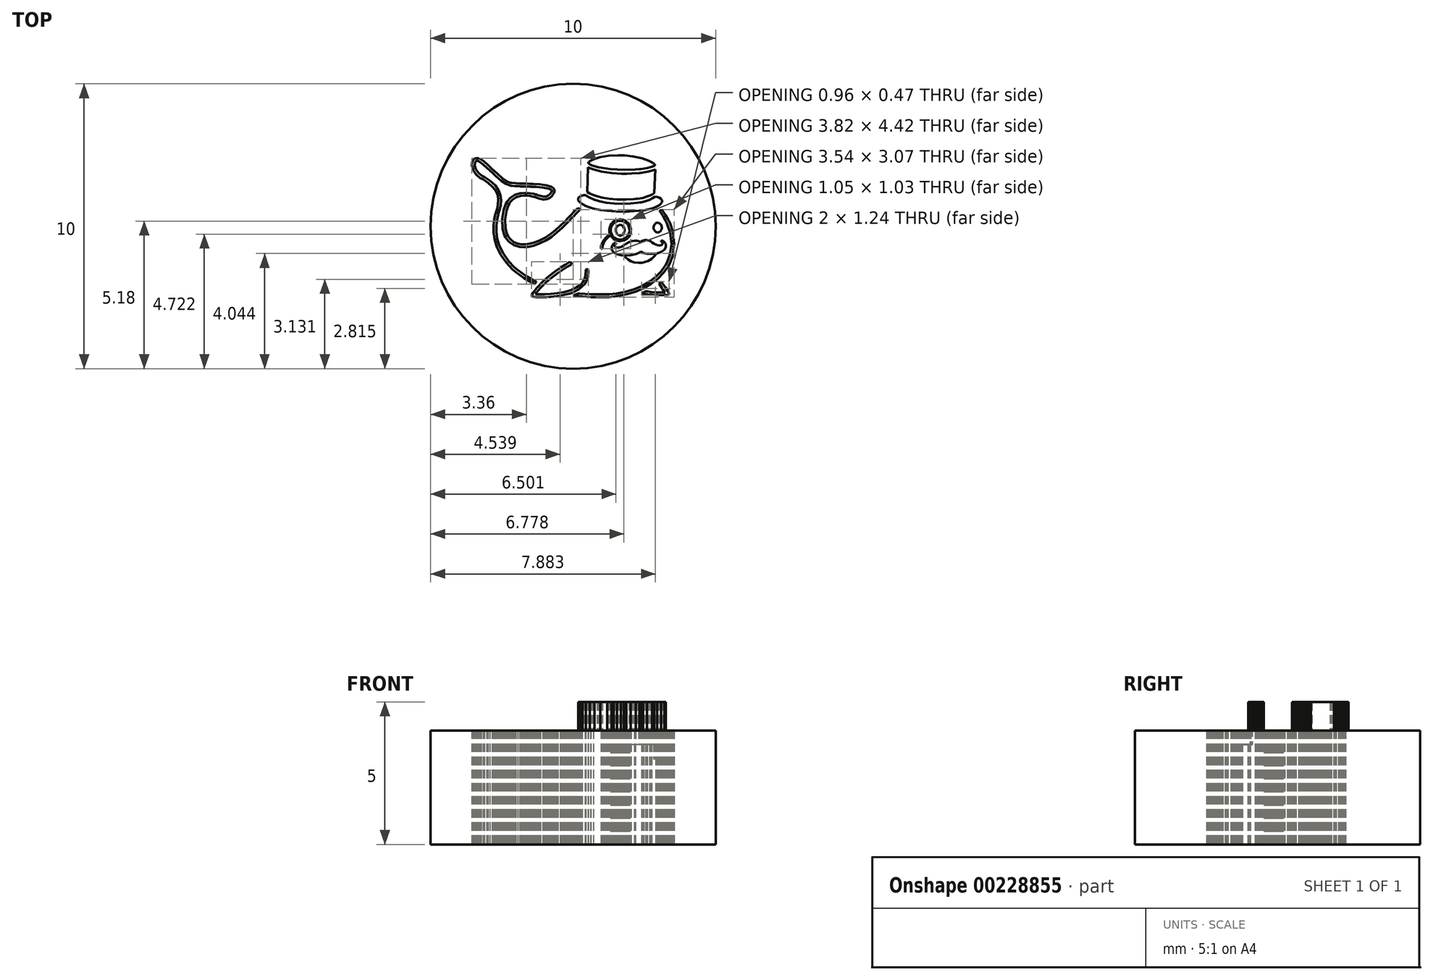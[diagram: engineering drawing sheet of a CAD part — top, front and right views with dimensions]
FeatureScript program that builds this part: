
annotation { "Feature Type Name" : "Feature", "Feature Type Description" : "" }
export const myFeature = defineFeature(function(context is Context, id is Id, definition is map)
    precondition{}
    {
        {
            var Q0;
            Q0=qCreatedBy(makeId("Top.planeOp"),FACE);
            var sketch = newSketch(context, id + "F0", { "sketchPlane" : qUnion([Q0])});
            skLineSegment(sketch, "E0", {"start": v(2.92, -0.96) * mm, "end": v(2.85, -1.06) * mm});
            skLineSegment(sketch, "E1", {"start": v(2.85, -1.06) * mm, "end": v(2.75, -1.15) * mm});
            skLineSegment(sketch, "E2", {"start": v(2.75, -1.15) * mm, "end": v(2.62, -1.22) * mm});
            skLineSegment(sketch, "E3", {"start": v(2.62, -1.22) * mm, "end": v(2.5, -1.26) * mm});
            skLineSegment(sketch, "E4", {"start": v(2.5, -1.26) * mm, "end": v(2.46, -1.27) * mm});
            skLineSegment(sketch, "E5", {"start": v(2.46, -1.27) * mm, "end": v(2.42, -1.28) * mm});
            skLineSegment(sketch, "E6", {"start": v(2.42, -1.28) * mm, "end": v(2.3, -1.29) * mm});
            skLineSegment(sketch, "E7", {"start": v(2.3, -1.29) * mm, "end": v(2.15, -1.27) * mm});
            skLineSegment(sketch, "E8", {"start": v(2.15, -1.27) * mm, "end": v(2.03, -1.23) * mm});
            skLineSegment(sketch, "E9", {"start": v(2.03, -1.23) * mm, "end": v(1.93, -1.17) * mm});
            skLineSegment(sketch, "E10", {"start": v(1.93, -1.17) * mm, "end": v(1.84, -1.1) * mm});
            skLineSegment(sketch, "E11", {"start": v(-1.26, -2.49) * mm, "end": v(-1.26, -2.49) * mm});
            skLineSegment(sketch, "E12", {"start": v(-1.26, -2.49) * mm, "end": v(-1.28, -2.48) * mm});
            skLineSegment(sketch, "E13", {"start": v(-1.28, -2.48) * mm, "end": v(-1.29, -2.48) * mm});
            skLineSegment(sketch, "E14", {"start": v(-1.29, -2.48) * mm, "end": v(-1.3, -2.48) * mm});
            skLineSegment(sketch, "E15", {"start": v(-1.3, -2.48) * mm, "end": v(-1.37, -2.48) * mm});
            skLineSegment(sketch, "E16", {"start": v(-1.37, -2.48) * mm, "end": v(-1.42, -2.47) * mm});
            skLineSegment(sketch, "E17", {"start": v(-1.42, -2.47) * mm, "end": v(-1.44, -2.46) * mm});
            skLineSegment(sketch, "E18", {"start": v(-1.44, -2.46) * mm, "end": v(-1.45, -2.45) * mm});
            skLineSegment(sketch, "E19", {"start": v(-1.45, -2.45) * mm, "end": v(-1.45, -2.45) * mm});
            skLineSegment(sketch, "E20", {"start": v(-1.45, -2.45) * mm, "end": v(-1.46, -2.42) * mm});
            skLineSegment(sketch, "E21", {"start": v(-1.46, -2.42) * mm, "end": v(-1.45, -2.4) * mm});
            skLineSegment(sketch, "E22", {"start": v(-1.45, -2.4) * mm, "end": v(-1.4, -2.34) * mm});
            skLineSegment(sketch, "E23", {"start": v(-1.4, -2.34) * mm, "end": v(-1.27, -2.16) * mm});
            skLineSegment(sketch, "E24", {"start": v(-1.27, -2.16) * mm, "end": v(-1.07, -1.94) * mm});
            skLineSegment(sketch, "E25", {"start": v(-1.07, -1.94) * mm, "end": v(-0.85, -1.75) * mm});
            skLineSegment(sketch, "E26", {"start": v(-0.85, -1.75) * mm, "end": v(-0.63, -1.58) * mm});
            skLineSegment(sketch, "E27", {"start": v(-0.63, -1.58) * mm, "end": v(-0.43, -1.45) * mm});
            skLineSegment(sketch, "E28", {"start": v(-0.43, -1.45) * mm, "end": v(-0.26, -1.34) * mm});
            skLineSegment(sketch, "E29", {"start": v(-0.26, -1.34) * mm, "end": v(-0.15, -1.28) * mm});
            skLineSegment(sketch, "E30", {"start": v(-0.15, -1.28) * mm, "end": v(-0.1, -1.25) * mm});
            skLineSegment(sketch, "E31", {"start": v(-0.1, -1.25) * mm, "end": v(-0.1, -1.25) * mm});
            skLineSegment(sketch, "E32", {"start": v(-0.1, -1.25) * mm, "end": v(-0.05, -1.33) * mm});
            skLineSegment(sketch, "E33", {"start": v(-0.05, -1.33) * mm, "end": v(-0.05, -1.34) * mm});
            skLineSegment(sketch, "E34", {"start": v(-0.05, -1.34) * mm, "end": v(-0.1, -1.36) * mm});
            skLineSegment(sketch, "E35", {"start": v(-0.1, -1.36) * mm, "end": v(-0.2, -1.42) * mm});
            skLineSegment(sketch, "E36", {"start": v(-0.2, -1.42) * mm, "end": v(-0.35, -1.5) * mm});
            skLineSegment(sketch, "E37", {"start": v(-0.35, -1.5) * mm, "end": v(-0.53, -1.63) * mm});
            skLineSegment(sketch, "E38", {"start": v(-0.53, -1.63) * mm, "end": v(-0.74, -1.79) * mm});
            skLineSegment(sketch, "E39", {"start": v(-0.74, -1.79) * mm, "end": v(-0.95, -1.97) * mm});
            skLineSegment(sketch, "E40", {"start": v(-0.95, -1.97) * mm, "end": v(-1.15, -2.17) * mm});
            skLineSegment(sketch, "E41", {"start": v(-1.15, -2.17) * mm, "end": v(-1.28, -2.33) * mm});
            skLineSegment(sketch, "E42", {"start": v(-1.28, -2.33) * mm, "end": v(-1.32, -2.39) * mm});
            skLineSegment(sketch, "E43", {"start": v(-1.32, -2.39) * mm, "end": v(-1.29, -2.39) * mm});
            skLineSegment(sketch, "E44", {"start": v(-1.29, -2.39) * mm, "end": v(-1.19, -2.4) * mm});
            skLineSegment(sketch, "E45", {"start": v(-1.19, -2.4) * mm, "end": v(-1, -2.4) * mm});
            skLineSegment(sketch, "E46", {"start": v(-1, -2.4) * mm, "end": v(-0.8, -2.38) * mm});
            skLineSegment(sketch, "E47", {"start": v(-0.8, -2.38) * mm, "end": v(-0.56, -2.36) * mm});
            skLineSegment(sketch, "E48", {"start": v(-0.56, -2.36) * mm, "end": v(-0.32, -2.31) * mm});
            skLineSegment(sketch, "E49", {"start": v(-0.32, -2.31) * mm, "end": v(-0.09, -2.25) * mm});
            skLineSegment(sketch, "E50", {"start": v(-0.09, -2.25) * mm, "end": v(0.12, -2.15) * mm});
            skLineSegment(sketch, "E51", {"start": v(0.12, -2.15) * mm, "end": v(0.25, -2.07) * mm});
            skLineSegment(sketch, "E52", {"start": v(0.25, -2.07) * mm, "end": v(0.29, -2.03) * mm});
            skLineSegment(sketch, "E53", {"start": v(0.29, -2.03) * mm, "end": v(0.32, -2) * mm});
            skLineSegment(sketch, "E54", {"start": v(0.32, -2) * mm, "end": v(0.42, -1.8) * mm});
            skLineSegment(sketch, "E55", {"start": v(0.42, -1.8) * mm, "end": v(0.44, -1.57) * mm});
            skLineSegment(sketch, "E56", {"start": v(0.44, -1.57) * mm, "end": v(0.43, -1.52) * mm});
            skLineSegment(sketch, "E57", {"start": v(0.43, -1.52) * mm, "end": v(0.53, -1.5) * mm});
            skLineSegment(sketch, "E58", {"start": v(0.53, -1.5) * mm, "end": v(0.54, -1.57) * mm});
            skLineSegment(sketch, "E59", {"start": v(0.54, -1.57) * mm, "end": v(0.53, -1.78) * mm});
            skLineSegment(sketch, "E60", {"start": v(0.53, -1.78) * mm, "end": v(0.42, -2.02) * mm});
            skLineSegment(sketch, "E61", {"start": v(0.42, -2.02) * mm, "end": v(0.2, -2.21) * mm});
            skLineSegment(sketch, "E62", {"start": v(0.2, -2.21) * mm, "end": v(-0.03, -2.33) * mm});
            skLineSegment(sketch, "E63", {"start": v(-0.03, -2.33) * mm, "end": v(-0.12, -2.36) * mm});
            skLineSegment(sketch, "E64", {"start": v(-0.12, -2.36) * mm, "end": v(-0.17, -2.38) * mm});
            skLineSegment(sketch, "E65", {"start": v(-0.17, -2.38) * mm, "end": v(-0.34, -2.42) * mm});
            skLineSegment(sketch, "E66", {"start": v(-0.34, -2.42) * mm, "end": v(-0.57, -2.45) * mm});
            skLineSegment(sketch, "E67", {"start": v(-0.57, -2.45) * mm, "end": v(-0.78, -2.48) * mm});
            skLineSegment(sketch, "E68", {"start": v(-0.78, -2.48) * mm, "end": v(-0.92, -2.48) * mm});
            skLineSegment(sketch, "E69", {"start": v(-0.92, -2.48) * mm, "end": v(-0.97, -2.49) * mm});
            skLineSegment(sketch, "E70", {"start": v(-0.97, -2.49) * mm, "end": v(-1, -2.49) * mm});
            skLineSegment(sketch, "E71", {"start": v(-1, -2.49) * mm, "end": v(-1.14, -2.49) * mm});
            skLineSegment(sketch, "E72", {"start": v(-1.14, -2.49) * mm, "end": v(-1.24, -2.49) * mm});
            skLineSegment(sketch, "E73", {"start": v(-1.24, -2.49) * mm, "end": v(-1.26, -2.49) * mm});
            skLineSegment(sketch, "E74", {"start": v(3.36, -2.34) * mm, "end": v(3.34, -2.3) * mm});
            skLineSegment(sketch, "E75", {"start": v(3.34, -2.3) * mm, "end": v(3.23, -2.14) * mm});
            skLineSegment(sketch, "E76", {"start": v(3.23, -2.14) * mm, "end": v(3.12, -1.98) * mm});
            skLineSegment(sketch, "E77", {"start": v(3.12, -1.98) * mm, "end": v(3.1, -1.95) * mm});
            skLineSegment(sketch, "E78", {"start": v(3.1, -1.95) * mm, "end": v(3.09, -1.96) * mm});
            skLineSegment(sketch, "E79", {"start": v(3.09, -1.96) * mm, "end": v(3.02, -2.01) * mm});
            skLineSegment(sketch, "E80", {"start": v(3.02, -2.01) * mm, "end": v(3.01, -2.02) * mm});
            skLineSegment(sketch, "E81", {"start": v(3.01, -2.02) * mm, "end": v(3.03, -2.04) * mm});
            skLineSegment(sketch, "E82", {"start": v(3.03, -2.04) * mm, "end": v(3.2, -2.3) * mm});
            skLineSegment(sketch, "E83", {"start": v(3.2, -2.3) * mm, "end": v(3.22, -2.32) * mm});
            skLineSegment(sketch, "E84", {"start": v(3.22, -2.32) * mm, "end": v(3.2, -2.32) * mm});
            skLineSegment(sketch, "E85", {"start": v(3.2, -2.32) * mm, "end": v(3.1, -2.32) * mm});
            skLineSegment(sketch, "E86", {"start": v(3.1, -2.32) * mm, "end": v(2.94, -2.32) * mm});
            skLineSegment(sketch, "E87", {"start": v(2.94, -2.32) * mm, "end": v(2.75, -2.3) * mm});
            skLineSegment(sketch, "E88", {"start": v(2.75, -2.3) * mm, "end": v(2.6, -2.3) * mm});
            skLineSegment(sketch, "E89", {"start": v(2.6, -2.3) * mm, "end": v(2.55, -2.28) * mm});
            skLineSegment(sketch, "E90", {"start": v(2.55, -2.28) * mm, "end": v(2.54, -2.3) * mm});
            skLineSegment(sketch, "E91", {"start": v(2.54, -2.3) * mm, "end": v(2.41, -2.35) * mm});
            skLineSegment(sketch, "E92", {"start": v(2.41, -2.35) * mm, "end": v(2.4, -2.35) * mm});
            skLineSegment(sketch, "E93", {"start": v(2.4, -2.35) * mm, "end": v(2.43, -2.36) * mm});
            skLineSegment(sketch, "E94", {"start": v(2.43, -2.36) * mm, "end": v(2.7, -2.4) * mm});
            skLineSegment(sketch, "E95", {"start": v(2.7, -2.4) * mm, "end": v(2.73, -2.4) * mm});
            skLineSegment(sketch, "E96", {"start": v(2.73, -2.4) * mm, "end": v(2.75, -2.4) * mm});
            skLineSegment(sketch, "E97", {"start": v(2.75, -2.4) * mm, "end": v(2.91, -2.42) * mm});
            skLineSegment(sketch, "E98", {"start": v(2.91, -2.42) * mm, "end": v(2.93, -2.42) * mm});
            skLineSegment(sketch, "E99", {"start": v(2.93, -2.42) * mm, "end": v(2.96, -2.42) * mm});
            skLineSegment(sketch, "E100", {"start": v(2.96, -2.42) * mm, "end": v(3.09, -2.42) * mm});
            skLineSegment(sketch, "E101", {"start": v(3.09, -2.42) * mm, "end": v(3.19, -2.42) * mm});
            skLineSegment(sketch, "E102", {"start": v(3.19, -2.42) * mm, "end": v(3.2, -2.42) * mm});
            skLineSegment(sketch, "E103", {"start": v(3.2, -2.42) * mm, "end": v(3.22, -2.42) * mm});
            skLineSegment(sketch, "E104", {"start": v(3.22, -2.42) * mm, "end": v(3.28, -2.42) * mm});
            skLineSegment(sketch, "E105", {"start": v(3.28, -2.42) * mm, "end": v(3.32, -2.41) * mm});
            skLineSegment(sketch, "E106", {"start": v(3.32, -2.41) * mm, "end": v(3.35, -2.4) * mm});
            skLineSegment(sketch, "E107", {"start": v(3.35, -2.4) * mm, "end": v(3.36, -2.4) * mm});
            skLineSegment(sketch, "E108", {"start": v(3.36, -2.4) * mm, "end": v(3.36, -2.39) * mm});
            skLineSegment(sketch, "E109", {"start": v(3.36, -2.39) * mm, "end": v(3.36, -2.39) * mm});
            skLineSegment(sketch, "E110", {"start": v(3.36, -2.39) * mm, "end": v(3.36, -2.35) * mm});
            skLineSegment(sketch, "E111", {"start": v(3.36, -2.35) * mm, "end": v(3.36, -2.34) * mm});
            skLineSegment(sketch, "E112", {"start": v(0.27, 0.6) * mm, "end": v(0.26, 0.6) * mm});
            skLineSegment(sketch, "E113", {"start": v(0.26, 0.6) * mm, "end": v(0.18, 0.64) * mm});
            skLineSegment(sketch, "E114", {"start": v(0.18, 0.64) * mm, "end": v(0.17, 0.64) * mm});
            skLineSegment(sketch, "E115", {"start": v(0.17, 0.64) * mm, "end": v(0.15, 0.62) * mm});
            skLineSegment(sketch, "E116", {"start": v(0.15, 0.62) * mm, "end": v(0.09, 0.56) * mm});
            skLineSegment(sketch, "E117", {"start": v(0.09, 0.56) * mm, "end": v(0.02, 0.5) * mm});
            skLineSegment(sketch, "E118", {"start": v(0.02, 0.5) * mm, "end": v(-0.05, 0.42) * mm});
            skLineSegment(sketch, "E119", {"start": v(-0.05, 0.42) * mm, "end": v(-0.12, 0.35) * mm});
            skLineSegment(sketch, "E120", {"start": v(-0.12, 0.35) * mm, "end": v(-0.14, 0.33) * mm});
            skLineSegment(sketch, "E121", {"start": v(-0.14, 0.33) * mm, "end": v(-0.18, 0.29) * mm});
            skLineSegment(sketch, "E122", {"start": v(-0.18, 0.29) * mm, "end": v(-0.3, 0.17) * mm});
            skLineSegment(sketch, "E123", {"start": v(-0.3, 0.17) * mm, "end": v(-0.45, 0.01) * mm});
            skLineSegment(sketch, "E124", {"start": v(-0.45, 0.01) * mm, "end": v(-0.62, -0.14) * mm});
            skLineSegment(sketch, "E125", {"start": v(-0.62, -0.14) * mm, "end": v(-0.8, -0.28) * mm});
            skLineSegment(sketch, "E126", {"start": v(-0.8, -0.28) * mm, "end": v(-1, -0.4) * mm});
            skLineSegment(sketch, "E127", {"start": v(-1, -0.4) * mm, "end": v(-1.2, -0.51) * mm});
            skLineSegment(sketch, "E128", {"start": v(-1.2, -0.51) * mm, "end": v(-1.41, -0.59) * mm});
            skLineSegment(sketch, "E129", {"start": v(-1.41, -0.59) * mm, "end": v(-1.59, -0.62) * mm});
            skLineSegment(sketch, "E130", {"start": v(-1.59, -0.62) * mm, "end": v(-1.65, -0.63) * mm});
            skLineSegment(sketch, "E131", {"start": v(-1.65, -0.63) * mm, "end": v(-1.66, -0.63) * mm});
            skLineSegment(sketch, "E132", {"start": v(-1.66, -0.63) * mm, "end": v(-1.77, -0.64) * mm});
            skLineSegment(sketch, "E133", {"start": v(-1.77, -0.64) * mm, "end": v(-1.78, -0.63) * mm});
            skLineSegment(sketch, "E134", {"start": v(-1.78, -0.63) * mm, "end": v(-1.82, -0.63) * mm});
            skLineSegment(sketch, "E135", {"start": v(-1.82, -0.63) * mm, "end": v(-1.95, -0.61) * mm});
            skLineSegment(sketch, "E136", {"start": v(-1.95, -0.61) * mm, "end": v(-2.08, -0.55) * mm});
            skLineSegment(sketch, "E137", {"start": v(-2.08, -0.55) * mm, "end": v(-2.2, -0.46) * mm});
            skLineSegment(sketch, "E138", {"start": v(-2.2, -0.46) * mm, "end": v(-2.27, -0.37) * mm});
            skLineSegment(sketch, "E139", {"start": v(-2.27, -0.37) * mm, "end": v(-2.29, -0.34) * mm});
            skLineSegment(sketch, "E140", {"start": v(-2.29, -0.34) * mm, "end": v(-2.32, -0.28) * mm});
            skLineSegment(sketch, "E141", {"start": v(-2.32, -0.28) * mm, "end": v(-2.38, -0.07) * mm});
            skLineSegment(sketch, "E142", {"start": v(-2.38, -0.07) * mm, "end": v(-2.4, 0.24) * mm});
            skLineSegment(sketch, "E143", {"start": v(-2.4, 0.24) * mm, "end": v(-2.34, 0.54) * mm});
            skLineSegment(sketch, "E144", {"start": v(-2.34, 0.54) * mm, "end": v(-2.27, 0.74) * mm});
            skLineSegment(sketch, "E145", {"start": v(-2.27, 0.74) * mm, "end": v(-2.24, 0.8) * mm});
            skLineSegment(sketch, "E146", {"start": v(-2.24, 0.8) * mm, "end": v(-2.22, 0.83) * mm});
            skLineSegment(sketch, "E147", {"start": v(-2.22, 0.83) * mm, "end": v(-2.14, 0.93) * mm});
            skLineSegment(sketch, "E148", {"start": v(-2.14, 0.93) * mm, "end": v(-2, 1.01) * mm});
            skLineSegment(sketch, "E149", {"start": v(-2, 1.01) * mm, "end": v(-1.84, 1.06) * mm});
            skLineSegment(sketch, "E150", {"start": v(-1.84, 1.06) * mm, "end": v(-1.7, 1.08) * mm});
            skLineSegment(sketch, "E151", {"start": v(-1.7, 1.08) * mm, "end": v(-1.64, 1.08) * mm});
            skLineSegment(sketch, "E152", {"start": v(-1.64, 1.08) * mm, "end": v(-1.61, 1.07) * mm});
            skLineSegment(sketch, "E153", {"start": v(-1.61, 1.07) * mm, "end": v(-1.52, 1.06) * mm});
            skLineSegment(sketch, "E154", {"start": v(-1.52, 1.06) * mm, "end": v(-1.42, 1.05) * mm});
            skLineSegment(sketch, "E155", {"start": v(-1.42, 1.05) * mm, "end": v(-1.35, 1.03) * mm});
            skLineSegment(sketch, "E156", {"start": v(-1.35, 1.03) * mm, "end": v(-1.33, 1.02) * mm});
            skLineSegment(sketch, "E157", {"start": v(-1.33, 1.02) * mm, "end": v(-1.33, 1.02) * mm});
            skLineSegment(sketch, "E158", {"start": v(-1.33, 1.02) * mm, "end": v(-1.3, 1.01) * mm});
            skLineSegment(sketch, "E159", {"start": v(-1.3, 1.01) * mm, "end": v(-1.28, 1) * mm});
            skLineSegment(sketch, "E160", {"start": v(-1.28, 1) * mm, "end": v(-1.17, 0.97) * mm});
            skLineSegment(sketch, "E161", {"start": v(-1.17, 0.97) * mm, "end": v(-1.05, 0.94) * mm});
            skLineSegment(sketch, "E162", {"start": v(-1.05, 0.94) * mm, "end": v(-1.03, 0.94) * mm});
            skLineSegment(sketch, "E163", {"start": v(-1.03, 0.94) * mm, "end": v(-1, 0.94) * mm});
            skLineSegment(sketch, "E164", {"start": v(-1, 0.94) * mm, "end": v(-0.92, 0.95) * mm});
            skLineSegment(sketch, "E165", {"start": v(-0.92, 0.95) * mm, "end": v(-0.83, 0.99) * mm});
            skLineSegment(sketch, "E166", {"start": v(-0.83, 0.99) * mm, "end": v(-0.75, 1.06) * mm});
            skLineSegment(sketch, "E167", {"start": v(-0.75, 1.06) * mm, "end": v(-0.7, 1.13) * mm});
            skLineSegment(sketch, "E168", {"start": v(-0.7, 1.13) * mm, "end": v(-0.68, 1.15) * mm});
            skLineSegment(sketch, "E169", {"start": v(-0.68, 1.15) * mm, "end": v(-0.67, 1.16) * mm});
            skLineSegment(sketch, "E170", {"start": v(-0.67, 1.16) * mm, "end": v(-0.66, 1.2) * mm});
            skLineSegment(sketch, "E171", {"start": v(-0.66, 1.2) * mm, "end": v(-0.65, 1.24) * mm});
            skLineSegment(sketch, "E172", {"start": v(-0.65, 1.24) * mm, "end": v(-0.66, 1.28) * mm});
            skLineSegment(sketch, "E173", {"start": v(-0.66, 1.28) * mm, "end": v(-0.66, 1.3) * mm});
            skLineSegment(sketch, "E174", {"start": v(-0.66, 1.3) * mm, "end": v(-0.67, 1.3) * mm});
            skLineSegment(sketch, "E175", {"start": v(-0.67, 1.3) * mm, "end": v(-0.68, 1.33) * mm});
            skLineSegment(sketch, "E176", {"start": v(-0.68, 1.33) * mm, "end": v(-0.76, 1.39) * mm});
            skLineSegment(sketch, "E177", {"start": v(-0.76, 1.39) * mm, "end": v(-0.93, 1.44) * mm});
            skLineSegment(sketch, "E178", {"start": v(-0.93, 1.44) * mm, "end": v(-1.17, 1.47) * mm});
            skLineSegment(sketch, "E179", {"start": v(-1.17, 1.47) * mm, "end": v(-1.4, 1.48) * mm});
            skLineSegment(sketch, "E180", {"start": v(-1.4, 1.48) * mm, "end": v(-1.47, 1.49) * mm});
            skLineSegment(sketch, "E181", {"start": v(-1.47, 1.49) * mm, "end": v(-1.49, 1.49) * mm});
            skLineSegment(sketch, "E182", {"start": v(-1.49, 1.49) * mm, "end": v(-1.65, 1.5) * mm});
            skLineSegment(sketch, "E183", {"start": v(-1.65, 1.5) * mm, "end": v(-1.66, 1.5) * mm});
            skLineSegment(sketch, "E184", {"start": v(-1.66, 1.5) * mm, "end": v(-1.68, 1.5) * mm});
            skLineSegment(sketch, "E185", {"start": v(-1.68, 1.5) * mm, "end": v(-1.82, 1.5) * mm});
            skLineSegment(sketch, "E186", {"start": v(-1.82, 1.5) * mm, "end": v(-1.84, 1.5) * mm});
            skLineSegment(sketch, "E187", {"start": v(-1.84, 1.5) * mm, "end": v(-1.86, 1.5) * mm});
            skLineSegment(sketch, "E188", {"start": v(-1.86, 1.5) * mm, "end": v(-2, 1.5) * mm});
            skLineSegment(sketch, "E189", {"start": v(-2, 1.5) * mm, "end": v(-2.14, 1.52) * mm});
            skLineSegment(sketch, "E190", {"start": v(-2.14, 1.52) * mm, "end": v(-2.17, 1.52) * mm});
            skLineSegment(sketch, "E191", {"start": v(-2.17, 1.52) * mm, "end": v(-2.2, 1.53) * mm});
            skLineSegment(sketch, "E192", {"start": v(-2.2, 1.53) * mm, "end": v(-2.32, 1.58) * mm});
            skLineSegment(sketch, "E193", {"start": v(-2.32, 1.58) * mm, "end": v(-2.48, 1.7) * mm});
            skLineSegment(sketch, "E194", {"start": v(-2.48, 1.7) * mm, "end": v(-2.66, 1.84) * mm});
            skLineSegment(sketch, "E195", {"start": v(-2.66, 1.84) * mm, "end": v(-2.78, 1.96) * mm});
            skLineSegment(sketch, "E196", {"start": v(-2.78, 1.96) * mm, "end": v(-2.83, 2) * mm});
            skLineSegment(sketch, "E197", {"start": v(-2.83, 2) * mm, "end": v(-2.86, 2.04) * mm});
            skLineSegment(sketch, "E198", {"start": v(-2.86, 2.04) * mm, "end": v(-2.98, 2.15) * mm});
            skLineSegment(sketch, "E199", {"start": v(-2.98, 2.15) * mm, "end": v(-3.13, 2.27) * mm});
            skLineSegment(sketch, "E200", {"start": v(-3.13, 2.27) * mm, "end": v(-3.25, 2.36) * mm});
            skLineSegment(sketch, "E201", {"start": v(-3.25, 2.36) * mm, "end": v(-3.34, 2.39) * mm});
            skLineSegment(sketch, "E202", {"start": v(-3.34, 2.39) * mm, "end": v(-3.37, 2.39) * mm});
            skLineSegment(sketch, "E203", {"start": v(-3.37, 2.39) * mm, "end": v(-3.38, 2.4) * mm});
            skLineSegment(sketch, "E204", {"start": v(-3.38, 2.4) * mm, "end": v(-3.4, 2.39) * mm});
            skLineSegment(sketch, "E205", {"start": v(-3.4, 2.39) * mm, "end": v(-3.45, 2.37) * mm});
            skLineSegment(sketch, "E206", {"start": v(-3.45, 2.37) * mm, "end": v(-3.49, 2.34) * mm});
            skLineSegment(sketch, "E207", {"start": v(-3.49, 2.34) * mm, "end": v(-3.52, 2.3) * mm});
            skLineSegment(sketch, "E208", {"start": v(-3.52, 2.3) * mm, "end": v(-3.52, 2.28) * mm});
            skLineSegment(sketch, "E209", {"start": v(-3.52, 2.28) * mm, "end": v(-3.54, 2.25) * mm});
            skLineSegment(sketch, "E210", {"start": v(-3.54, 2.25) * mm, "end": v(-3.55, 2.14) * mm});
            skLineSegment(sketch, "E211", {"start": v(-3.55, 2.14) * mm, "end": v(-3.5, 1.97) * mm});
            skLineSegment(sketch, "E212", {"start": v(-3.5, 1.97) * mm, "end": v(-3.4, 1.81) * mm});
            skLineSegment(sketch, "E213", {"start": v(-3.4, 1.81) * mm, "end": v(-3.28, 1.7) * mm});
            skLineSegment(sketch, "E214", {"start": v(-3.28, 1.7) * mm, "end": v(-3.23, 1.68) * mm});
            skLineSegment(sketch, "E215", {"start": v(-3.23, 1.68) * mm, "end": v(-3.17, 1.65) * mm});
            skLineSegment(sketch, "E216", {"start": v(-3.17, 1.65) * mm, "end": v(-2.99, 1.53) * mm});
            skLineSegment(sketch, "E217", {"start": v(-2.99, 1.53) * mm, "end": v(-2.81, 1.38) * mm});
            skLineSegment(sketch, "E218", {"start": v(-2.81, 1.38) * mm, "end": v(-2.7, 1.23) * mm});
            skLineSegment(sketch, "E219", {"start": v(-2.7, 1.23) * mm, "end": v(-2.64, 1.07) * mm});
            skLineSegment(sketch, "E220", {"start": v(-2.64, 1.07) * mm, "end": v(-2.63, 0.92) * mm});
            skLineSegment(sketch, "E221", {"start": v(-2.63, 0.92) * mm, "end": v(-2.64, 0.77) * mm});
            skLineSegment(sketch, "E222", {"start": v(-2.64, 0.77) * mm, "end": v(-2.67, 0.61) * mm});
            skLineSegment(sketch, "E223", {"start": v(-2.67, 0.61) * mm, "end": v(-2.7, 0.5) * mm});
            skLineSegment(sketch, "E224", {"start": v(-2.7, 0.5) * mm, "end": v(-2.71, 0.46) * mm});
            skLineSegment(sketch, "E225", {"start": v(-2.71, 0.46) * mm, "end": v(-2.73, 0.42) * mm});
            skLineSegment(sketch, "E226", {"start": v(-2.73, 0.42) * mm, "end": v(-2.74, 0.37) * mm});
            skLineSegment(sketch, "E227", {"start": v(-2.74, 0.37) * mm, "end": v(-2.77, 0.24) * mm});
            skLineSegment(sketch, "E228", {"start": v(-2.77, 0.24) * mm, "end": v(-2.8, 0.03) * mm});
            skLineSegment(sketch, "E229", {"start": v(-2.8, 0.03) * mm, "end": v(-2.8, -0.2) * mm});
            skLineSegment(sketch, "E230", {"start": v(-2.8, -0.2) * mm, "end": v(-2.76, -0.45) * mm});
            skLineSegment(sketch, "E231", {"start": v(-2.76, -0.45) * mm, "end": v(-2.68, -0.72) * mm});
            skLineSegment(sketch, "E232", {"start": v(-2.68, -0.72) * mm, "end": v(-2.54, -1) * mm});
            skLineSegment(sketch, "E233", {"start": v(-2.54, -1) * mm, "end": v(-2.34, -1.29) * mm});
            skLineSegment(sketch, "E234", {"start": v(-2.34, -1.29) * mm, "end": v(-2.13, -1.5) * mm});
            skLineSegment(sketch, "E235", {"start": v(-2.13, -1.5) * mm, "end": v(-2.06, -1.57) * mm});
            skLineSegment(sketch, "E236", {"start": v(-2.06, -1.57) * mm, "end": v(-2, -1.62) * mm});
            skLineSegment(sketch, "E237", {"start": v(-2, -1.62) * mm, "end": v(-1.73, -1.82) * mm});
            skLineSegment(sketch, "E238", {"start": v(-1.73, -1.82) * mm, "end": v(-1.42, -2) * mm});
            skLineSegment(sketch, "E239", {"start": v(-1.42, -2) * mm, "end": v(-1.35, -2.03) * mm});
            skLineSegment(sketch, "E240", {"start": v(-1.35, -2.03) * mm, "end": v(-1.35, -2.02) * mm});
            skLineSegment(sketch, "E241", {"start": v(-1.35, -2.02) * mm, "end": v(-1.3, -1.96) * mm});
            skLineSegment(sketch, "E242", {"start": v(-1.3, -1.96) * mm, "end": v(-1.3, -1.95) * mm});
            skLineSegment(sketch, "E243", {"start": v(-1.3, -1.95) * mm, "end": v(-1.36, -1.92) * mm});
            skLineSegment(sketch, "E244", {"start": v(-1.36, -1.92) * mm, "end": v(-1.67, -1.74) * mm});
            skLineSegment(sketch, "E245", {"start": v(-1.67, -1.74) * mm, "end": v(-1.94, -1.54) * mm});
            skLineSegment(sketch, "E246", {"start": v(-1.94, -1.54) * mm, "end": v(-2, -1.5) * mm});
            skLineSegment(sketch, "E247", {"start": v(-2, -1.5) * mm, "end": v(-2.06, -1.44) * mm});
            skLineSegment(sketch, "E248", {"start": v(-2.06, -1.44) * mm, "end": v(-2.26, -1.23) * mm});
            skLineSegment(sketch, "E249", {"start": v(-2.26, -1.23) * mm, "end": v(-2.45, -0.96) * mm});
            skLineSegment(sketch, "E250", {"start": v(-2.45, -0.96) * mm, "end": v(-2.59, -0.7) * mm});
            skLineSegment(sketch, "E251", {"start": v(-2.59, -0.7) * mm, "end": v(-2.66, -0.44) * mm});
            skLineSegment(sketch, "E252", {"start": v(-2.66, -0.44) * mm, "end": v(-2.7, -0.2) * mm});
            skLineSegment(sketch, "E253", {"start": v(-2.7, -0.2) * mm, "end": v(-2.7, 0.03) * mm});
            skLineSegment(sketch, "E254", {"start": v(-2.7, 0.03) * mm, "end": v(-2.67, 0.22) * mm});
            skLineSegment(sketch, "E255", {"start": v(-2.67, 0.22) * mm, "end": v(-2.64, 0.35) * mm});
            skLineSegment(sketch, "E256", {"start": v(-2.64, 0.35) * mm, "end": v(-2.63, 0.39) * mm});
            skLineSegment(sketch, "E257", {"start": v(-2.63, 0.39) * mm, "end": v(-2.62, 0.43) * mm});
            skLineSegment(sketch, "E258", {"start": v(-2.62, 0.43) * mm, "end": v(-2.6, 0.47) * mm});
            skLineSegment(sketch, "E259", {"start": v(-2.6, 0.47) * mm, "end": v(-2.58, 0.59) * mm});
            skLineSegment(sketch, "E260", {"start": v(-2.58, 0.59) * mm, "end": v(-2.54, 0.75) * mm});
            skLineSegment(sketch, "E261", {"start": v(-2.54, 0.75) * mm, "end": v(-2.53, 0.92) * mm});
            skLineSegment(sketch, "E262", {"start": v(-2.53, 0.92) * mm, "end": v(-2.55, 1.09) * mm});
            skLineSegment(sketch, "E263", {"start": v(-2.55, 1.09) * mm, "end": v(-2.61, 1.26) * mm});
            skLineSegment(sketch, "E264", {"start": v(-2.61, 1.26) * mm, "end": v(-2.73, 1.43) * mm});
            skLineSegment(sketch, "E265", {"start": v(-2.73, 1.43) * mm, "end": v(-2.92, 1.6) * mm});
            skLineSegment(sketch, "E266", {"start": v(-2.92, 1.6) * mm, "end": v(-3.11, 1.73) * mm});
            skLineSegment(sketch, "E267", {"start": v(-3.11, 1.73) * mm, "end": v(-3.18, 1.76) * mm});
            skLineSegment(sketch, "E268", {"start": v(-3.18, 1.76) * mm, "end": v(-3.22, 1.79) * mm});
            skLineSegment(sketch, "E269", {"start": v(-3.22, 1.79) * mm, "end": v(-3.33, 1.88) * mm});
            skLineSegment(sketch, "E270", {"start": v(-3.33, 1.88) * mm, "end": v(-3.42, 2) * mm});
            skLineSegment(sketch, "E271", {"start": v(-3.42, 2) * mm, "end": v(-3.45, 2.14) * mm});
            skLineSegment(sketch, "E272", {"start": v(-3.45, 2.14) * mm, "end": v(-3.45, 2.22) * mm});
            skLineSegment(sketch, "E273", {"start": v(-3.45, 2.22) * mm, "end": v(-3.44, 2.24) * mm});
            skLineSegment(sketch, "E274", {"start": v(-3.44, 2.24) * mm, "end": v(-3.43, 2.25) * mm});
            skLineSegment(sketch, "E275", {"start": v(-3.43, 2.25) * mm, "end": v(-3.4, 2.29) * mm});
            skLineSegment(sketch, "E276", {"start": v(-3.4, 2.29) * mm, "end": v(-3.38, 2.3) * mm});
            skLineSegment(sketch, "E277", {"start": v(-3.38, 2.3) * mm, "end": v(-3.37, 2.3) * mm});
            skLineSegment(sketch, "E278", {"start": v(-3.37, 2.3) * mm, "end": v(-3.35, 2.3) * mm});
            skLineSegment(sketch, "E279", {"start": v(-3.35, 2.3) * mm, "end": v(-3.28, 2.26) * mm});
            skLineSegment(sketch, "E280", {"start": v(-3.28, 2.26) * mm, "end": v(-3.16, 2.18) * mm});
            skLineSegment(sketch, "E281", {"start": v(-3.16, 2.18) * mm, "end": v(-3.03, 2.06) * mm});
            skLineSegment(sketch, "E282", {"start": v(-3.03, 2.06) * mm, "end": v(-2.93, 1.96) * mm});
            skLineSegment(sketch, "E283", {"start": v(-2.93, 1.96) * mm, "end": v(-2.9, 1.93) * mm});
            skLineSegment(sketch, "E284", {"start": v(-2.9, 1.93) * mm, "end": v(-2.85, 1.89) * mm});
            skLineSegment(sketch, "E285", {"start": v(-2.85, 1.89) * mm, "end": v(-2.7, 1.76) * mm});
            skLineSegment(sketch, "E286", {"start": v(-2.7, 1.76) * mm, "end": v(-2.53, 1.6) * mm});
            skLineSegment(sketch, "E287", {"start": v(-2.53, 1.6) * mm, "end": v(-2.35, 1.48) * mm});
            skLineSegment(sketch, "E288", {"start": v(-2.35, 1.48) * mm, "end": v(-2.22, 1.43) * mm});
            skLineSegment(sketch, "E289", {"start": v(-2.22, 1.43) * mm, "end": v(-2.18, 1.43) * mm});
            skLineSegment(sketch, "E290", {"start": v(-2.18, 1.43) * mm, "end": v(-2.16, 1.42) * mm});
            skLineSegment(sketch, "E291", {"start": v(-2.16, 1.42) * mm, "end": v(-2.04, 1.41) * mm});
            skLineSegment(sketch, "E292", {"start": v(-2.04, 1.41) * mm, "end": v(-1.88, 1.4) * mm});
            skLineSegment(sketch, "E293", {"start": v(-1.88, 1.4) * mm, "end": v(-1.84, 1.4) * mm});
            skLineSegment(sketch, "E294", {"start": v(-1.84, 1.4) * mm, "end": v(-1.83, 1.4) * mm});
            skLineSegment(sketch, "E295", {"start": v(-1.83, 1.4) * mm, "end": v(-1.68, 1.4) * mm});
            skLineSegment(sketch, "E296", {"start": v(-1.68, 1.4) * mm, "end": v(-1.67, 1.4) * mm});
            skLineSegment(sketch, "E297", {"start": v(-1.67, 1.4) * mm, "end": v(-1.65, 1.4) * mm});
            skLineSegment(sketch, "E298", {"start": v(-1.65, 1.4) * mm, "end": v(-1.5, 1.4) * mm});
            skLineSegment(sketch, "E299", {"start": v(-1.5, 1.4) * mm, "end": v(-1.48, 1.39) * mm});
            skLineSegment(sketch, "E300", {"start": v(-1.48, 1.39) * mm, "end": v(-1.43, 1.39) * mm});
            skLineSegment(sketch, "E301", {"start": v(-1.43, 1.39) * mm, "end": v(-1.3, 1.38) * mm});
            skLineSegment(sketch, "E302", {"start": v(-1.3, 1.38) * mm, "end": v(-1.07, 1.36) * mm});
            skLineSegment(sketch, "E303", {"start": v(-1.07, 1.36) * mm, "end": v(-0.86, 1.32) * mm});
            skLineSegment(sketch, "E304", {"start": v(-0.86, 1.32) * mm, "end": v(-0.77, 1.28) * mm});
            skLineSegment(sketch, "E305", {"start": v(-0.77, 1.28) * mm, "end": v(-0.75, 1.26) * mm});
            skLineSegment(sketch, "E306", {"start": v(-0.75, 1.26) * mm, "end": v(-0.75, 1.26) * mm});
            skLineSegment(sketch, "E307", {"start": v(-0.75, 1.26) * mm, "end": v(-0.75, 1.24) * mm});
            skLineSegment(sketch, "E308", {"start": v(-0.75, 1.24) * mm, "end": v(-0.76, 1.2) * mm});
            skLineSegment(sketch, "E309", {"start": v(-0.76, 1.2) * mm, "end": v(-0.76, 1.2) * mm});
            skLineSegment(sketch, "E310", {"start": v(-0.76, 1.2) * mm, "end": v(-0.77, 1.18) * mm});
            skLineSegment(sketch, "E311", {"start": v(-0.77, 1.18) * mm, "end": v(-0.82, 1.13) * mm});
            skLineSegment(sketch, "E312", {"start": v(-0.82, 1.13) * mm, "end": v(-0.88, 1.07) * mm});
            skLineSegment(sketch, "E313", {"start": v(-0.88, 1.07) * mm, "end": v(-0.95, 1.05) * mm});
            skLineSegment(sketch, "E314", {"start": v(-0.95, 1.05) * mm, "end": v(-1, 1.04) * mm});
            skLineSegment(sketch, "E315", {"start": v(-1, 1.04) * mm, "end": v(-1.02, 1.04) * mm});
            skLineSegment(sketch, "E316", {"start": v(-1.02, 1.04) * mm, "end": v(-1.04, 1.04) * mm});
            skLineSegment(sketch, "E317", {"start": v(-1.04, 1.04) * mm, "end": v(-1.15, 1.06) * mm});
            skLineSegment(sketch, "E318", {"start": v(-1.15, 1.06) * mm, "end": v(-1.25, 1.1) * mm});
            skLineSegment(sketch, "E319", {"start": v(-1.25, 1.1) * mm, "end": v(-1.27, 1.1) * mm});
            skLineSegment(sketch, "E320", {"start": v(-1.27, 1.1) * mm, "end": v(-1.3, 1.11) * mm});
            skLineSegment(sketch, "E321", {"start": v(-1.3, 1.11) * mm, "end": v(-1.3, 1.11) * mm});
            skLineSegment(sketch, "E322", {"start": v(-1.3, 1.11) * mm, "end": v(-1.32, 1.12) * mm});
            skLineSegment(sketch, "E323", {"start": v(-1.32, 1.12) * mm, "end": v(-1.4, 1.14) * mm});
            skLineSegment(sketch, "E324", {"start": v(-1.4, 1.14) * mm, "end": v(-1.5, 1.16) * mm});
            skLineSegment(sketch, "E325", {"start": v(-1.5, 1.16) * mm, "end": v(-1.6, 1.17) * mm});
            skLineSegment(sketch, "E326", {"start": v(-1.6, 1.17) * mm, "end": v(-1.64, 1.17) * mm});
            skLineSegment(sketch, "E327", {"start": v(-1.64, 1.17) * mm, "end": v(-1.7, 1.17) * mm});
            skLineSegment(sketch, "E328", {"start": v(-1.7, 1.17) * mm, "end": v(-1.86, 1.16) * mm});
            skLineSegment(sketch, "E329", {"start": v(-1.86, 1.16) * mm, "end": v(-2.05, 1.1) * mm});
            skLineSegment(sketch, "E330", {"start": v(-2.05, 1.1) * mm, "end": v(-2.2, 1) * mm});
            skLineSegment(sketch, "E331", {"start": v(-2.2, 1) * mm, "end": v(-2.3, 0.89) * mm});
            skLineSegment(sketch, "E332", {"start": v(-2.3, 0.89) * mm, "end": v(-2.32, 0.85) * mm});
            skLineSegment(sketch, "E333", {"start": v(-2.32, 0.85) * mm, "end": v(-2.36, 0.78) * mm});
            skLineSegment(sketch, "E334", {"start": v(-2.36, 0.78) * mm, "end": v(-2.43, 0.57) * mm});
            skLineSegment(sketch, "E335", {"start": v(-2.43, 0.57) * mm, "end": v(-2.49, 0.25) * mm});
            skLineSegment(sketch, "E336", {"start": v(-2.49, 0.25) * mm, "end": v(-2.47, -0.08) * mm});
            skLineSegment(sketch, "E337", {"start": v(-2.47, -0.08) * mm, "end": v(-2.41, -0.32) * mm});
            skLineSegment(sketch, "E338", {"start": v(-2.41, -0.32) * mm, "end": v(-2.37, -0.39) * mm});
            skLineSegment(sketch, "E339", {"start": v(-2.37, -0.39) * mm, "end": v(-2.35, -0.43) * mm});
            skLineSegment(sketch, "E340", {"start": v(-2.35, -0.43) * mm, "end": v(-2.25, -0.55) * mm});
            skLineSegment(sketch, "E341", {"start": v(-2.25, -0.55) * mm, "end": v(-2.08, -0.66) * mm});
            skLineSegment(sketch, "E342", {"start": v(-2.08, -0.66) * mm, "end": v(-1.87, -0.72) * mm});
            skLineSegment(sketch, "E343", {"start": v(-1.87, -0.72) * mm, "end": v(-1.7, -0.73) * mm});
            skLineSegment(sketch, "E344", {"start": v(-1.7, -0.73) * mm, "end": v(-1.64, -0.73) * mm});
            skLineSegment(sketch, "E345", {"start": v(-1.64, -0.73) * mm, "end": v(-1.57, -0.72) * mm});
            skLineSegment(sketch, "E346", {"start": v(-1.57, -0.72) * mm, "end": v(-1.4, -0.68) * mm});
            skLineSegment(sketch, "E347", {"start": v(-1.4, -0.68) * mm, "end": v(-1.16, -0.6) * mm});
            skLineSegment(sketch, "E348", {"start": v(-1.16, -0.6) * mm, "end": v(-0.95, -0.5) * mm});
            skLineSegment(sketch, "E349", {"start": v(-0.95, -0.5) * mm, "end": v(-0.75, -0.37) * mm});
            skLineSegment(sketch, "E350", {"start": v(-0.75, -0.37) * mm, "end": v(-0.57, -0.22) * mm});
            skLineSegment(sketch, "E351", {"start": v(-0.57, -0.22) * mm, "end": v(-0.4, -0.06) * mm});
            skLineSegment(sketch, "E352", {"start": v(-0.4, -0.06) * mm, "end": v(-0.23, 0.1) * mm});
            skLineSegment(sketch, "E353", {"start": v(-0.23, 0.1) * mm, "end": v(-0.1, 0.22) * mm});
            skLineSegment(sketch, "E354", {"start": v(-0.1, 0.22) * mm, "end": v(-0.07, 0.26) * mm});
            skLineSegment(sketch, "E355", {"start": v(-0.07, 0.26) * mm, "end": v(-0.05, 0.29) * mm});
            skLineSegment(sketch, "E356", {"start": v(-0.05, 0.29) * mm, "end": v(0.02, 0.36) * mm});
            skLineSegment(sketch, "E357", {"start": v(0.02, 0.36) * mm, "end": v(0.1, 0.44) * mm});
            skLineSegment(sketch, "E358", {"start": v(0.1, 0.44) * mm, "end": v(0.18, 0.52) * mm});
            skLineSegment(sketch, "E359", {"start": v(0.18, 0.52) * mm, "end": v(0.25, 0.58) * mm});
            skLineSegment(sketch, "E360", {"start": v(0.25, 0.58) * mm, "end": v(0.27, 0.6) * mm});
            skLineSegment(sketch, "E361", {"start": v(3.12, 0.58) * mm, "end": v(3.1, 0.58) * mm});
            skLineSegment(sketch, "E362", {"start": v(3.1, 0.58) * mm, "end": v(3.03, 0.55) * mm});
            skLineSegment(sketch, "E363", {"start": v(3.03, 0.55) * mm, "end": v(3.02, 0.54) * mm});
            skLineSegment(sketch, "E364", {"start": v(3.02, 0.54) * mm, "end": v(3.04, 0.52) * mm});
            skLineSegment(sketch, "E365", {"start": v(3.04, 0.52) * mm, "end": v(3.15, 0.36) * mm});
            skLineSegment(sketch, "E366", {"start": v(3.15, 0.36) * mm, "end": v(3.25, 0.2) * mm});
            skLineSegment(sketch, "E367", {"start": v(3.25, 0.2) * mm, "end": v(3.26, 0.16) * mm});
            skLineSegment(sketch, "E368", {"start": v(3.26, 0.16) * mm, "end": v(3.3, 0.07) * mm});
            skLineSegment(sketch, "E369", {"start": v(3.3, 0.07) * mm, "end": v(3.4, -0.24) * mm});
            skLineSegment(sketch, "E370", {"start": v(3.4, -0.24) * mm, "end": v(3.45, -0.63) * mm});
            skLineSegment(sketch, "E371", {"start": v(3.45, -0.63) * mm, "end": v(3.4, -1) * mm});
            skLineSegment(sketch, "E372", {"start": v(3.4, -1) * mm, "end": v(3.3, -1.29) * mm});
            skLineSegment(sketch, "E373", {"start": v(3.3, -1.29) * mm, "end": v(3.24, -1.37) * mm});
            skLineSegment(sketch, "E374", {"start": v(3.24, -1.37) * mm, "end": v(3.2, -1.43) * mm});
            skLineSegment(sketch, "E375", {"start": v(3.2, -1.43) * mm, "end": v(3.09, -1.58) * mm});
            skLineSegment(sketch, "E376", {"start": v(3.09, -1.58) * mm, "end": v(2.9, -1.78) * mm});
            skLineSegment(sketch, "E377", {"start": v(2.9, -1.78) * mm, "end": v(2.68, -1.95) * mm});
            skLineSegment(sketch, "E378", {"start": v(2.68, -1.95) * mm, "end": v(2.43, -2.1) * mm});
            skLineSegment(sketch, "E379", {"start": v(2.43, -2.1) * mm, "end": v(2.15, -2.21) * mm});
            skLineSegment(sketch, "E380", {"start": v(2.15, -2.21) * mm, "end": v(1.85, -2.3) * mm});
            skLineSegment(sketch, "E381", {"start": v(1.85, -2.3) * mm, "end": v(1.52, -2.36) * mm});
            skLineSegment(sketch, "E382", {"start": v(1.52, -2.36) * mm, "end": v(1.27, -2.39) * mm});
            skLineSegment(sketch, "E383", {"start": v(1.27, -2.39) * mm, "end": v(1.18, -2.4) * mm});
            skLineSegment(sketch, "E384", {"start": v(1.18, -2.4) * mm, "end": v(1.14, -2.4) * mm});
            skLineSegment(sketch, "E385", {"start": v(1.14, -2.4) * mm, "end": v(0.71, -2.4) * mm});
            skLineSegment(sketch, "E386", {"start": v(0.71, -2.4) * mm, "end": v(0.67, -2.4) * mm});
            skLineSegment(sketch, "E387", {"start": v(0.67, -2.4) * mm, "end": v(0.63, -2.4) * mm});
            skLineSegment(sketch, "E388", {"start": v(0.63, -2.4) * mm, "end": v(0.22, -2.36) * mm});
            skLineSegment(sketch, "E389", {"start": v(0.22, -2.36) * mm, "end": v(0.18, -2.35) * mm});
            skLineSegment(sketch, "E390", {"start": v(0.18, -2.35) * mm, "end": v(0.17, -2.36) * mm});
            skLineSegment(sketch, "E391", {"start": v(0.17, -2.36) * mm, "end": v(0.02, -2.42) * mm});
            skLineSegment(sketch, "E392", {"start": v(0.02, -2.42) * mm, "end": v(0, -2.43) * mm});
            skLineSegment(sketch, "E393", {"start": v(0, -2.43) * mm, "end": v(0.06, -2.44) * mm});
            skLineSegment(sketch, "E394", {"start": v(0.06, -2.44) * mm, "end": v(0.61, -2.49) * mm});
            skLineSegment(sketch, "E395", {"start": v(0.61, -2.49) * mm, "end": v(0.67, -2.49) * mm});
            skLineSegment(sketch, "E396", {"start": v(0.67, -2.49) * mm, "end": v(0.7, -2.5) * mm});
            skLineSegment(sketch, "E397", {"start": v(0.7, -2.5) * mm, "end": v(1.14, -2.49) * mm});
            skLineSegment(sketch, "E398", {"start": v(1.14, -2.49) * mm, "end": v(1.18, -2.49) * mm});
            skLineSegment(sketch, "E399", {"start": v(1.18, -2.49) * mm, "end": v(1.27, -2.48) * mm});
            skLineSegment(sketch, "E400", {"start": v(1.27, -2.48) * mm, "end": v(1.54, -2.46) * mm});
            skLineSegment(sketch, "E401", {"start": v(1.54, -2.46) * mm, "end": v(1.87, -2.4) * mm});
            skLineSegment(sketch, "E402", {"start": v(1.87, -2.4) * mm, "end": v(2.19, -2.3) * mm});
            skLineSegment(sketch, "E403", {"start": v(2.19, -2.3) * mm, "end": v(2.48, -2.18) * mm});
            skLineSegment(sketch, "E404", {"start": v(2.48, -2.18) * mm, "end": v(2.74, -2.02) * mm});
            skLineSegment(sketch, "E405", {"start": v(2.74, -2.02) * mm, "end": v(2.97, -1.85) * mm});
            skLineSegment(sketch, "E406", {"start": v(2.97, -1.85) * mm, "end": v(3.16, -1.64) * mm});
            skLineSegment(sketch, "E407", {"start": v(3.16, -1.64) * mm, "end": v(3.29, -1.48) * mm});
            skLineSegment(sketch, "E408", {"start": v(3.29, -1.48) * mm, "end": v(3.32, -1.42) * mm});
            skLineSegment(sketch, "E409", {"start": v(3.32, -1.42) * mm, "end": v(3.38, -1.33) * mm});
            skLineSegment(sketch, "E410", {"start": v(3.38, -1.33) * mm, "end": v(3.49, -1.04) * mm});
            skLineSegment(sketch, "E411", {"start": v(3.49, -1.04) * mm, "end": v(3.55, -0.63) * mm});
            skLineSegment(sketch, "E412", {"start": v(3.55, -0.63) * mm, "end": v(3.5, -0.22) * mm});
            skLineSegment(sketch, "E413", {"start": v(3.5, -0.22) * mm, "end": v(3.4, 0.1) * mm});
            skLineSegment(sketch, "E414", {"start": v(3.4, 0.1) * mm, "end": v(3.35, 0.2) * mm});
            skLineSegment(sketch, "E415", {"start": v(3.35, 0.2) * mm, "end": v(3.33, 0.24) * mm});
            skLineSegment(sketch, "E416", {"start": v(3.33, 0.24) * mm, "end": v(3.24, 0.4) * mm});
            skLineSegment(sketch, "E417", {"start": v(3.24, 0.4) * mm, "end": v(3.14, 0.55) * mm});
            skLineSegment(sketch, "E418", {"start": v(3.14, 0.55) * mm, "end": v(3.12, 0.58) * mm});
            skLineSegment(sketch, "E419", {"start": v(2.37, -0.9) * mm, "end": v(2.33, -0.92) * mm});
            skLineSegment(sketch, "E420", {"start": v(2.33, -0.92) * mm, "end": v(2.2, -0.98) * mm});
            skLineSegment(sketch, "E421", {"start": v(2.2, -0.98) * mm, "end": v(2.02, -1.02) * mm});
            skLineSegment(sketch, "E422", {"start": v(2.02, -1.02) * mm, "end": v(1.87, -1.03) * mm});
            skLineSegment(sketch, "E423", {"start": v(1.87, -1.03) * mm, "end": v(1.81, -1.03) * mm});
            skLineSegment(sketch, "E424", {"start": v(1.81, -1.03) * mm, "end": v(1.78, -1.03) * mm});
            skLineSegment(sketch, "E425", {"start": v(1.78, -1.03) * mm, "end": v(1.68, -1.02) * mm});
            skLineSegment(sketch, "E426", {"start": v(1.68, -1.02) * mm, "end": v(1.54, -0.98) * mm});
            skLineSegment(sketch, "E427", {"start": v(1.54, -0.98) * mm, "end": v(1.42, -0.92) * mm});
            skLineSegment(sketch, "E428", {"start": v(1.42, -0.92) * mm, "end": v(1.36, -0.83) * mm});
            skLineSegment(sketch, "E429", {"start": v(1.36, -0.83) * mm, "end": v(1.36, -0.8) * mm});
            skLineSegment(sketch, "E430", {"start": v(1.36, -0.8) * mm, "end": v(1.35, -0.79) * mm});
            skLineSegment(sketch, "E431", {"start": v(1.35, -0.79) * mm, "end": v(1.35, -0.73) * mm});
            skLineSegment(sketch, "E432", {"start": v(1.35, -0.73) * mm, "end": v(1.38, -0.67) * mm});
            skLineSegment(sketch, "E433", {"start": v(1.38, -0.67) * mm, "end": v(1.4, -0.63) * mm});
            skLineSegment(sketch, "E434", {"start": v(1.4, -0.63) * mm, "end": v(1.43, -0.6) * mm});
            skLineSegment(sketch, "E435", {"start": v(1.43, -0.6) * mm, "end": v(1.44, -0.6) * mm});
            skLineSegment(sketch, "E436", {"start": v(1.44, -0.6) * mm, "end": v(1.44, -0.6) * mm});
            skLineSegment(sketch, "E437", {"start": v(1.44, -0.6) * mm, "end": v(1.46, -0.6) * mm});
            skLineSegment(sketch, "E438", {"start": v(1.46, -0.6) * mm, "end": v(1.46, -0.6) * mm});
            skLineSegment(sketch, "E439", {"start": v(1.46, -0.6) * mm, "end": v(1.48, -0.58) * mm});
            skLineSegment(sketch, "E440", {"start": v(1.48, -0.58) * mm, "end": v(1.48, -0.58) * mm});
            skLineSegment(sketch, "E441", {"start": v(1.48, -0.58) * mm, "end": v(1.5, -0.58) * mm});
            skLineSegment(sketch, "E442", {"start": v(1.5, -0.58) * mm, "end": v(1.5, -0.6) * mm});
            skLineSegment(sketch, "E443", {"start": v(1.5, -0.6) * mm, "end": v(1.5, -0.6) * mm});
            skLineSegment(sketch, "E444", {"start": v(1.5, -0.6) * mm, "end": v(1.5, -0.61) * mm});
            skLineSegment(sketch, "E445", {"start": v(1.5, -0.61) * mm, "end": v(1.49, -0.64) * mm});
            skLineSegment(sketch, "E446", {"start": v(1.49, -0.64) * mm, "end": v(1.49, -0.64) * mm});
            skLineSegment(sketch, "E447", {"start": v(1.49, -0.64) * mm, "end": v(1.48, -0.65) * mm});
            skLineSegment(sketch, "E448", {"start": v(1.48, -0.65) * mm, "end": v(1.46, -0.68) * mm});
            skLineSegment(sketch, "E449", {"start": v(1.46, -0.68) * mm, "end": v(1.46, -0.7) * mm});
            skLineSegment(sketch, "E450", {"start": v(1.46, -0.7) * mm, "end": v(1.46, -0.7) * mm});
            skLineSegment(sketch, "E451", {"start": v(1.46, -0.7) * mm, "end": v(1.46, -0.71) * mm});
            skLineSegment(sketch, "E452", {"start": v(1.46, -0.71) * mm, "end": v(1.5, -0.74) * mm});
            skLineSegment(sketch, "E453", {"start": v(1.5, -0.74) * mm, "end": v(1.55, -0.75) * mm});
            skLineSegment(sketch, "E454", {"start": v(1.55, -0.75) * mm, "end": v(1.56, -0.75) * mm});
            skLineSegment(sketch, "E455", {"start": v(1.56, -0.75) * mm, "end": v(1.57, -0.75) * mm});
            skLineSegment(sketch, "E456", {"start": v(1.57, -0.75) * mm, "end": v(1.6, -0.75) * mm});
            skLineSegment(sketch, "E457", {"start": v(1.6, -0.75) * mm, "end": v(1.64, -0.74) * mm});
            skLineSegment(sketch, "E458", {"start": v(1.64, -0.74) * mm, "end": v(1.7, -0.72) * mm});
            skLineSegment(sketch, "E459", {"start": v(1.7, -0.72) * mm, "end": v(1.74, -0.7) * mm});
            skLineSegment(sketch, "E460", {"start": v(1.74, -0.7) * mm, "end": v(1.75, -0.68) * mm});
            skLineSegment(sketch, "E461", {"start": v(1.75, -0.68) * mm, "end": v(1.77, -0.68) * mm});
            skLineSegment(sketch, "E462", {"start": v(1.77, -0.68) * mm, "end": v(1.8, -0.66) * mm});
            skLineSegment(sketch, "E463", {"start": v(1.8, -0.66) * mm, "end": v(1.87, -0.6) * mm});
            skLineSegment(sketch, "E464", {"start": v(1.87, -0.6) * mm, "end": v(1.96, -0.55) * mm});
            skLineSegment(sketch, "E465", {"start": v(1.96, -0.55) * mm, "end": v(2.06, -0.52) * mm});
            skLineSegment(sketch, "E466", {"start": v(2.06, -0.52) * mm, "end": v(2.14, -0.5) * mm});
            skLineSegment(sketch, "E467", {"start": v(2.14, -0.5) * mm, "end": v(2.17, -0.5) * mm});
            skLineSegment(sketch, "E468", {"start": v(2.17, -0.5) * mm, "end": v(2.19, -0.5) * mm});
            skLineSegment(sketch, "E469", {"start": v(2.19, -0.5) * mm, "end": v(2.24, -0.51) * mm});
            skLineSegment(sketch, "E470", {"start": v(2.24, -0.51) * mm, "end": v(2.3, -0.52) * mm});
            skLineSegment(sketch, "E471", {"start": v(2.3, -0.52) * mm, "end": v(2.33, -0.54) * mm});
            skLineSegment(sketch, "E472", {"start": v(2.33, -0.54) * mm, "end": v(2.35, -0.55) * mm});
            skLineSegment(sketch, "E473", {"start": v(2.35, -0.55) * mm, "end": v(2.36, -0.56) * mm});
            skLineSegment(sketch, "E474", {"start": v(2.36, -0.56) * mm, "end": v(2.36, -0.55) * mm});
            skLineSegment(sketch, "E475", {"start": v(2.36, -0.55) * mm, "end": v(2.38, -0.53) * mm});
            skLineSegment(sketch, "E476", {"start": v(2.38, -0.53) * mm, "end": v(2.42, -0.51) * mm});
            skLineSegment(sketch, "E477", {"start": v(2.42, -0.51) * mm, "end": v(2.47, -0.5) * mm});
            skLineSegment(sketch, "E478", {"start": v(2.47, -0.5) * mm, "end": v(2.52, -0.49) * mm});
            skLineSegment(sketch, "E479", {"start": v(2.52, -0.49) * mm, "end": v(2.54, -0.49) * mm});
            skLineSegment(sketch, "E480", {"start": v(2.54, -0.49) * mm, "end": v(2.56, -0.49) * mm});
            skLineSegment(sketch, "E481", {"start": v(2.56, -0.49) * mm, "end": v(2.62, -0.5) * mm});
            skLineSegment(sketch, "E482", {"start": v(2.62, -0.5) * mm, "end": v(2.68, -0.5) * mm});
            skLineSegment(sketch, "E483", {"start": v(2.68, -0.5) * mm, "end": v(2.73, -0.54) * mm});
            skLineSegment(sketch, "E484", {"start": v(2.73, -0.54) * mm, "end": v(2.76, -0.56) * mm});
            skLineSegment(sketch, "E485", {"start": v(2.76, -0.56) * mm, "end": v(2.77, -0.57) * mm});
            skLineSegment(sketch, "E486", {"start": v(2.77, -0.57) * mm, "end": v(2.77, -0.57) * mm});
            skLineSegment(sketch, "E487", {"start": v(2.77, -0.57) * mm, "end": v(2.84, -0.62) * mm});
            skLineSegment(sketch, "E488", {"start": v(2.84, -0.62) * mm, "end": v(2.85, -0.62) * mm});
            skLineSegment(sketch, "E489", {"start": v(2.85, -0.62) * mm, "end": v(2.86, -0.63) * mm});
            skLineSegment(sketch, "E490", {"start": v(2.86, -0.63) * mm, "end": v(2.94, -0.66) * mm});
            skLineSegment(sketch, "E491", {"start": v(2.94, -0.66) * mm, "end": v(3.01, -0.67) * mm});
            skLineSegment(sketch, "E492", {"start": v(3.01, -0.67) * mm, "end": v(3.03, -0.67) * mm});
            skLineSegment(sketch, "E493", {"start": v(3.03, -0.67) * mm, "end": v(3.04, -0.67) * mm});
            skLineSegment(sketch, "E494", {"start": v(3.04, -0.67) * mm, "end": v(3.1, -0.66) * mm});
            skLineSegment(sketch, "E495", {"start": v(3.1, -0.66) * mm, "end": v(3.14, -0.63) * mm});
            skLineSegment(sketch, "E496", {"start": v(3.14, -0.63) * mm, "end": v(3.14, -0.62) * mm});
            skLineSegment(sketch, "E497", {"start": v(3.14, -0.62) * mm, "end": v(3.14, -0.62) * mm});
            skLineSegment(sketch, "E498", {"start": v(3.14, -0.62) * mm, "end": v(3.14, -0.6) * mm});
            skLineSegment(sketch, "E499", {"start": v(3.14, -0.6) * mm, "end": v(3.14, -0.6) * mm});
            skLineSegment(sketch, "E500", {"start": v(3.14, -0.6) * mm, "end": v(3.13, -0.57) * mm});
            skLineSegment(sketch, "E501", {"start": v(3.13, -0.57) * mm, "end": v(3.12, -0.56) * mm});
            skLineSegment(sketch, "E502", {"start": v(3.12, -0.56) * mm, "end": v(3.11, -0.55) * mm});
            skLineSegment(sketch, "E503", {"start": v(3.11, -0.55) * mm, "end": v(3.1, -0.55) * mm});
            skLineSegment(sketch, "E504", {"start": v(3.1, -0.55) * mm, "end": v(3.09, -0.53) * mm});
            skLineSegment(sketch, "E505", {"start": v(3.09, -0.53) * mm, "end": v(3.09, -0.52) * mm});
            skLineSegment(sketch, "E506", {"start": v(3.09, -0.52) * mm, "end": v(3.09, -0.51) * mm});
            skLineSegment(sketch, "E507", {"start": v(3.09, -0.51) * mm, "end": v(3.1, -0.5) * mm});
            skLineSegment(sketch, "E508", {"start": v(3.1, -0.5) * mm, "end": v(3.1, -0.5) * mm});
            skLineSegment(sketch, "E509", {"start": v(3.1, -0.5) * mm, "end": v(3.11, -0.5) * mm});
            skLineSegment(sketch, "E510", {"start": v(3.11, -0.5) * mm, "end": v(3.11, -0.5) * mm});
            skLineSegment(sketch, "E511", {"start": v(3.11, -0.5) * mm, "end": v(3.12, -0.5) * mm});
            skLineSegment(sketch, "E512", {"start": v(3.12, -0.5) * mm, "end": v(3.14, -0.5) * mm});
            skLineSegment(sketch, "E513", {"start": v(3.14, -0.5) * mm, "end": v(3.14, -0.5) * mm});
            skLineSegment(sketch, "E514", {"start": v(3.14, -0.5) * mm, "end": v(3.15, -0.5) * mm});
            skLineSegment(sketch, "E515", {"start": v(3.15, -0.5) * mm, "end": v(3.16, -0.51) * mm});
            skLineSegment(sketch, "E516", {"start": v(3.16, -0.51) * mm, "end": v(3.18, -0.53) * mm});
            skLineSegment(sketch, "E517", {"start": v(3.18, -0.53) * mm, "end": v(3.22, -0.57) * mm});
            skLineSegment(sketch, "E518", {"start": v(3.22, -0.57) * mm, "end": v(3.25, -0.62) * mm});
            skLineSegment(sketch, "E519", {"start": v(3.25, -0.62) * mm, "end": v(3.26, -0.69) * mm});
            skLineSegment(sketch, "E520", {"start": v(3.26, -0.69) * mm, "end": v(3.26, -0.7) * mm});
            skLineSegment(sketch, "E521", {"start": v(3.26, -0.7) * mm, "end": v(3.25, -0.74) * mm});
            skLineSegment(sketch, "E522", {"start": v(3.25, -0.74) * mm, "end": v(3.2, -0.82) * mm});
            skLineSegment(sketch, "E523", {"start": v(3.2, -0.82) * mm, "end": v(3.08, -0.9) * mm});
            skLineSegment(sketch, "E524", {"start": v(3.08, -0.9) * mm, "end": v(2.95, -0.95) * mm});
            skLineSegment(sketch, "E525", {"start": v(2.95, -0.95) * mm, "end": v(2.85, -0.96) * mm});
            skLineSegment(sketch, "E526", {"start": v(2.85, -0.96) * mm, "end": v(2.82, -0.97) * mm});
            skLineSegment(sketch, "E527", {"start": v(2.82, -0.97) * mm, "end": v(2.76, -0.97) * mm});
            skLineSegment(sketch, "E528", {"start": v(2.76, -0.97) * mm, "end": v(2.6, -0.96) * mm});
            skLineSegment(sketch, "E529", {"start": v(2.6, -0.96) * mm, "end": v(2.45, -0.93) * mm});
            skLineSegment(sketch, "E530", {"start": v(2.45, -0.93) * mm, "end": v(2.39, -0.9) * mm});
            skLineSegment(sketch, "E531", {"start": v(2.39, -0.9) * mm, "end": v(2.37, -0.9) * mm});
            skLineSegment(sketch, "E532", {"start": v(1.66, 0.19) * mm, "end": v(1.64, 0.19) * mm});
            skLineSegment(sketch, "E533", {"start": v(1.64, 0.19) * mm, "end": v(1.6, 0.18) * mm});
            skLineSegment(sketch, "E534", {"start": v(1.6, 0.18) * mm, "end": v(1.53, 0.17) * mm});
            skLineSegment(sketch, "E535", {"start": v(1.53, 0.17) * mm, "end": v(1.47, 0.14) * mm});
            skLineSegment(sketch, "E536", {"start": v(1.47, 0.14) * mm, "end": v(1.42, 0.1) * mm});
            skLineSegment(sketch, "E537", {"start": v(1.42, 0.1) * mm, "end": v(1.38, 0.05) * mm});
            skLineSegment(sketch, "E538", {"start": v(1.38, 0.05) * mm, "end": v(1.35, 0) * mm});
            skLineSegment(sketch, "E539", {"start": v(1.35, 0) * mm, "end": v(1.33, -0.06) * mm});
            skLineSegment(sketch, "E540", {"start": v(1.33, -0.06) * mm, "end": v(1.32, -0.11) * mm});
            skLineSegment(sketch, "E541", {"start": v(1.32, -0.11) * mm, "end": v(1.32, -0.13) * mm});
            skLineSegment(sketch, "E542", {"start": v(1.32, -0.13) * mm, "end": v(1.32, -0.14) * mm});
            skLineSegment(sketch, "E543", {"start": v(1.32, -0.14) * mm, "end": v(1.32, -0.2) * mm});
            skLineSegment(sketch, "E544", {"start": v(1.32, -0.2) * mm, "end": v(1.34, -0.26) * mm});
            skLineSegment(sketch, "E545", {"start": v(1.34, -0.26) * mm, "end": v(1.37, -0.31) * mm});
            skLineSegment(sketch, "E546", {"start": v(1.37, -0.31) * mm, "end": v(1.4, -0.36) * mm});
            skLineSegment(sketch, "E547", {"start": v(1.4, -0.36) * mm, "end": v(1.45, -0.4) * mm});
            skLineSegment(sketch, "E548", {"start": v(1.45, -0.4) * mm, "end": v(1.5, -0.44) * mm});
            skLineSegment(sketch, "E549", {"start": v(1.5, -0.44) * mm, "end": v(1.57, -0.46) * mm});
            skLineSegment(sketch, "E550", {"start": v(1.57, -0.46) * mm, "end": v(1.62, -0.47) * mm});
            skLineSegment(sketch, "E551", {"start": v(1.62, -0.47) * mm, "end": v(1.64, -0.47) * mm});
            skLineSegment(sketch, "E552", {"start": v(1.64, -0.47) * mm, "end": v(1.65, -0.47) * mm});
            skLineSegment(sketch, "E553", {"start": v(1.65, -0.47) * mm, "end": v(1.7, -0.47) * mm});
            skLineSegment(sketch, "E554", {"start": v(1.7, -0.47) * mm, "end": v(1.77, -0.45) * mm});
            skLineSegment(sketch, "E555", {"start": v(1.77, -0.45) * mm, "end": v(1.82, -0.42) * mm});
            skLineSegment(sketch, "E556", {"start": v(1.82, -0.42) * mm, "end": v(1.87, -0.38) * mm});
            skLineSegment(sketch, "E557", {"start": v(1.87, -0.38) * mm, "end": v(1.91, -0.33) * mm});
            skLineSegment(sketch, "E558", {"start": v(1.91, -0.33) * mm, "end": v(1.95, -0.28) * mm});
            skLineSegment(sketch, "E559", {"start": v(1.95, -0.28) * mm, "end": v(1.97, -0.22) * mm});
            skLineSegment(sketch, "E560", {"start": v(1.97, -0.22) * mm, "end": v(1.98, -0.17) * mm});
            skLineSegment(sketch, "E561", {"start": v(1.98, -0.17) * mm, "end": v(1.98, -0.15) * mm});
            skLineSegment(sketch, "E562", {"start": v(1.98, -0.15) * mm, "end": v(1.98, -0.14) * mm});
            skLineSegment(sketch, "E563", {"start": v(1.98, -0.14) * mm, "end": v(1.97, -0.09) * mm});
            skLineSegment(sketch, "E564", {"start": v(1.97, -0.09) * mm, "end": v(1.96, -0.02) * mm});
            skLineSegment(sketch, "E565", {"start": v(1.96, -0.02) * mm, "end": v(1.93, 0.03) * mm});
            skLineSegment(sketch, "E566", {"start": v(1.93, 0.03) * mm, "end": v(1.89, 0.08) * mm});
            skLineSegment(sketch, "E567", {"start": v(1.89, 0.08) * mm, "end": v(1.84, 0.13) * mm});
            skLineSegment(sketch, "E568", {"start": v(1.84, 0.13) * mm, "end": v(1.79, 0.16) * mm});
            skLineSegment(sketch, "E569", {"start": v(1.79, 0.16) * mm, "end": v(1.73, 0.18) * mm});
            skLineSegment(sketch, "E570", {"start": v(1.73, 0.18) * mm, "end": v(1.68, 0.19) * mm});
            skLineSegment(sketch, "E571", {"start": v(1.68, 0.19) * mm, "end": v(1.66, 0.19) * mm});
            skLineSegment(sketch, "E572", {"start": v(1.63, -0.52) * mm, "end": v(1.62, -0.52) * mm});
            skLineSegment(sketch, "E573", {"start": v(1.62, -0.52) * mm, "end": v(1.56, -0.5) * mm});
            skLineSegment(sketch, "E574", {"start": v(1.56, -0.5) * mm, "end": v(1.49, -0.48) * mm});
            skLineSegment(sketch, "E575", {"start": v(1.49, -0.48) * mm, "end": v(1.43, -0.45) * mm});
            skLineSegment(sketch, "E576", {"start": v(1.43, -0.45) * mm, "end": v(1.37, -0.4) * mm});
            skLineSegment(sketch, "E577", {"start": v(1.37, -0.4) * mm, "end": v(1.33, -0.34) * mm});
            skLineSegment(sketch, "E578", {"start": v(1.33, -0.34) * mm, "end": v(1.3, -0.27) * mm});
            skLineSegment(sketch, "E579", {"start": v(1.3, -0.27) * mm, "end": v(1.28, -0.2) * mm});
            skLineSegment(sketch, "E580", {"start": v(1.28, -0.2) * mm, "end": v(1.27, -0.15) * mm});
            skLineSegment(sketch, "E581", {"start": v(1.27, -0.15) * mm, "end": v(1.27, -0.13) * mm});
            skLineSegment(sketch, "E582", {"start": v(1.27, -0.13) * mm, "end": v(1.27, -0.1) * mm});
            skLineSegment(sketch, "E583", {"start": v(1.27, -0.1) * mm, "end": v(1.28, -0.05) * mm});
            skLineSegment(sketch, "E584", {"start": v(1.28, -0.05) * mm, "end": v(1.3, 0.02) * mm});
            skLineSegment(sketch, "E585", {"start": v(1.3, 0.02) * mm, "end": v(1.34, 0.08) * mm});
            skLineSegment(sketch, "E586", {"start": v(1.34, 0.08) * mm, "end": v(1.4, 0.14) * mm});
            skLineSegment(sketch, "E587", {"start": v(1.4, 0.14) * mm, "end": v(1.45, 0.18) * mm});
            skLineSegment(sketch, "E588", {"start": v(1.45, 0.18) * mm, "end": v(1.51, 0.21) * mm});
            skLineSegment(sketch, "E589", {"start": v(1.51, 0.21) * mm, "end": v(1.59, 0.23) * mm});
            skLineSegment(sketch, "E590", {"start": v(1.59, 0.23) * mm, "end": v(1.64, 0.24) * mm});
            skLineSegment(sketch, "E591", {"start": v(1.64, 0.24) * mm, "end": v(1.66, 0.24) * mm});
            skLineSegment(sketch, "E592", {"start": v(1.66, 0.24) * mm, "end": v(1.68, 0.24) * mm});
            skLineSegment(sketch, "E593", {"start": v(1.68, 0.24) * mm, "end": v(1.74, 0.23) * mm});
            skLineSegment(sketch, "E594", {"start": v(1.74, 0.23) * mm, "end": v(1.8, 0.2) * mm});
            skLineSegment(sketch, "E595", {"start": v(1.8, 0.2) * mm, "end": v(1.87, 0.16) * mm});
            skLineSegment(sketch, "E596", {"start": v(1.87, 0.16) * mm, "end": v(1.93, 0.12) * mm});
            skLineSegment(sketch, "E597", {"start": v(1.93, 0.12) * mm, "end": v(1.97, 0.06) * mm});
            skLineSegment(sketch, "E598", {"start": v(1.97, 0.06) * mm, "end": v(2, 0) * mm});
            skLineSegment(sketch, "E599", {"start": v(2, 0) * mm, "end": v(2.02, -0.08) * mm});
            skLineSegment(sketch, "E600", {"start": v(2.02, -0.08) * mm, "end": v(2.03, -0.14) * mm});
            skLineSegment(sketch, "E601", {"start": v(2.03, -0.14) * mm, "end": v(2.03, -0.15) * mm});
            skLineSegment(sketch, "E602", {"start": v(2.03, -0.15) * mm, "end": v(2.03, -0.17) * mm});
            skLineSegment(sketch, "E603", {"start": v(2.03, -0.17) * mm, "end": v(2.02, -0.23) * mm});
            skLineSegment(sketch, "E604", {"start": v(2.02, -0.23) * mm, "end": v(2, -0.3) * mm});
            skLineSegment(sketch, "E605", {"start": v(2, -0.3) * mm, "end": v(1.95, -0.36) * mm});
            skLineSegment(sketch, "E606", {"start": v(1.95, -0.36) * mm, "end": v(1.9, -0.42) * mm});
            skLineSegment(sketch, "E607", {"start": v(1.9, -0.42) * mm, "end": v(1.85, -0.46) * mm});
            skLineSegment(sketch, "E608", {"start": v(1.85, -0.46) * mm, "end": v(1.78, -0.5) * mm});
            skLineSegment(sketch, "E609", {"start": v(1.78, -0.5) * mm, "end": v(1.71, -0.51) * mm});
            skLineSegment(sketch, "E610", {"start": v(1.71, -0.51) * mm, "end": v(1.65, -0.52) * mm});
            skLineSegment(sketch, "E611", {"start": v(1.65, -0.52) * mm, "end": v(1.63, -0.52) * mm});
            skLineSegment(sketch, "E612", {"start": v(1, -0.8) * mm, "end": v(1, -0.8) * mm});
            skLineSegment(sketch, "E613", {"start": v(1, -0.8) * mm, "end": v(0.98, -0.79) * mm});
            skLineSegment(sketch, "E614", {"start": v(0.98, -0.79) * mm, "end": v(0.98, -0.77) * mm});
            skLineSegment(sketch, "E615", {"start": v(0.98, -0.77) * mm, "end": v(0.98, -0.77) * mm});
            skLineSegment(sketch, "E616", {"start": v(0.98, -0.77) * mm, "end": v(0.98, -0.75) * mm});
            skLineSegment(sketch, "E617", {"start": v(0.98, -0.75) * mm, "end": v(0.98, -0.7) * mm});
            skLineSegment(sketch, "E618", {"start": v(0.98, -0.7) * mm, "end": v(1, -0.65) * mm});
            skLineSegment(sketch, "E619", {"start": v(1, -0.65) * mm, "end": v(1.02, -0.58) * mm});
            skLineSegment(sketch, "E620", {"start": v(1.02, -0.58) * mm, "end": v(1.07, -0.5) * mm});
            skLineSegment(sketch, "E621", {"start": v(1.07, -0.5) * mm, "end": v(1.13, -0.42) * mm});
            skLineSegment(sketch, "E622", {"start": v(1.13, -0.42) * mm, "end": v(1.2, -0.34) * mm});
            skLineSegment(sketch, "E623", {"start": v(1.2, -0.34) * mm, "end": v(1.29, -0.3) * mm});
            skLineSegment(sketch, "E624", {"start": v(1.29, -0.3) * mm, "end": v(1.32, -0.28) * mm});
            skLineSegment(sketch, "E625", {"start": v(1.32, -0.28) * mm, "end": v(1.32, -0.28) * mm});
            skLineSegment(sketch, "E626", {"start": v(1.32, -0.28) * mm, "end": v(1.34, -0.28) * mm});
            skLineSegment(sketch, "E627", {"start": v(1.34, -0.28) * mm, "end": v(1.35, -0.29) * mm});
            skLineSegment(sketch, "E628", {"start": v(1.35, -0.29) * mm, "end": v(1.35, -0.3) * mm});
            skLineSegment(sketch, "E629", {"start": v(1.35, -0.3) * mm, "end": v(1.35, -0.3) * mm});
            skLineSegment(sketch, "E630", {"start": v(1.35, -0.3) * mm, "end": v(1.34, -0.32) * mm});
            skLineSegment(sketch, "E631", {"start": v(1.34, -0.32) * mm, "end": v(1.34, -0.32) * mm});
            skLineSegment(sketch, "E632", {"start": v(1.34, -0.32) * mm, "end": v(1.31, -0.34) * mm});
            skLineSegment(sketch, "E633", {"start": v(1.31, -0.34) * mm, "end": v(1.24, -0.38) * mm});
            skLineSegment(sketch, "E634", {"start": v(1.24, -0.38) * mm, "end": v(1.16, -0.45) * mm});
            skLineSegment(sketch, "E635", {"start": v(1.16, -0.45) * mm, "end": v(1.1, -0.52) * mm});
            skLineSegment(sketch, "E636", {"start": v(1.1, -0.52) * mm, "end": v(1.07, -0.6) * mm});
            skLineSegment(sketch, "E637", {"start": v(1.07, -0.6) * mm, "end": v(1.05, -0.66) * mm});
            skLineSegment(sketch, "E638", {"start": v(1.05, -0.66) * mm, "end": v(1.03, -0.72) * mm});
            skLineSegment(sketch, "E639", {"start": v(1.03, -0.72) * mm, "end": v(1.03, -0.75) * mm});
            skLineSegment(sketch, "E640", {"start": v(1.03, -0.75) * mm, "end": v(1.02, -0.77) * mm});
            skLineSegment(sketch, "E641", {"start": v(1.02, -0.77) * mm, "end": v(1.02, -0.77) * mm});
            skLineSegment(sketch, "E642", {"start": v(1.02, -0.77) * mm, "end": v(1.02, -0.79) * mm});
            skLineSegment(sketch, "E643", {"start": v(1.02, -0.79) * mm, "end": v(1, -0.8) * mm});
            skLineSegment(sketch, "E644", {"start": v(1.65, -0.33) * mm, "end": v(1.63, -0.32) * mm});
            skLineSegment(sketch, "E645", {"start": v(1.63, -0.32) * mm, "end": v(1.59, -0.3) * mm});
            skLineSegment(sketch, "E646", {"start": v(1.59, -0.3) * mm, "end": v(1.54, -0.27) * mm});
            skLineSegment(sketch, "E647", {"start": v(1.54, -0.27) * mm, "end": v(1.5, -0.21) * mm});
            skLineSegment(sketch, "E648", {"start": v(1.5, -0.21) * mm, "end": v(1.5, -0.16) * mm});
            skLineSegment(sketch, "E649", {"start": v(1.5, -0.16) * mm, "end": v(1.5, -0.15) * mm});
            skLineSegment(sketch, "E650", {"start": v(1.5, -0.15) * mm, "end": v(1.5, -0.13) * mm});
            skLineSegment(sketch, "E651", {"start": v(1.5, -0.13) * mm, "end": v(1.5, -0.08) * mm});
            skLineSegment(sketch, "E652", {"start": v(1.5, -0.08) * mm, "end": v(1.53, -0.02) * mm});
            skLineSegment(sketch, "E653", {"start": v(1.53, -0.02) * mm, "end": v(1.53, -0.02) * mm});
            skLineSegment(sketch, "E654", {"start": v(1.53, -0.02) * mm, "end": v(1.54, 0) * mm});
            skLineSegment(sketch, "E655", {"start": v(1.54, 0) * mm, "end": v(1.58, 0.03) * mm});
            skLineSegment(sketch, "E656", {"start": v(1.58, 0.03) * mm, "end": v(1.63, 0.04) * mm});
            skLineSegment(sketch, "E657", {"start": v(1.63, 0.04) * mm, "end": v(1.64, 0.04) * mm});
            skLineSegment(sketch, "E658", {"start": v(1.64, 0.04) * mm, "end": v(1.66, 0.04) * mm});
            skLineSegment(sketch, "E659", {"start": v(1.66, 0.04) * mm, "end": v(1.7, 0.03) * mm});
            skLineSegment(sketch, "E660", {"start": v(1.7, 0.03) * mm, "end": v(1.75, 0) * mm});
            skLineSegment(sketch, "E661", {"start": v(1.75, 0) * mm, "end": v(1.79, -0.06) * mm});
            skLineSegment(sketch, "E662", {"start": v(1.79, -0.06) * mm, "end": v(1.8, -0.12) * mm});
            skLineSegment(sketch, "E663", {"start": v(1.8, -0.12) * mm, "end": v(1.8, -0.14) * mm});
            skLineSegment(sketch, "E664", {"start": v(1.8, -0.14) * mm, "end": v(1.8, -0.15) * mm});
            skLineSegment(sketch, "E665", {"start": v(1.8, -0.15) * mm, "end": v(1.8, -0.2) * mm});
            skLineSegment(sketch, "E666", {"start": v(1.8, -0.2) * mm, "end": v(1.77, -0.26) * mm});
            skLineSegment(sketch, "E667", {"start": v(1.77, -0.26) * mm, "end": v(1.76, -0.27) * mm});
            skLineSegment(sketch, "E668", {"start": v(1.76, -0.27) * mm, "end": v(1.76, -0.27) * mm});
            skLineSegment(sketch, "E669", {"start": v(1.76, -0.27) * mm, "end": v(1.71, -0.3) * mm});
            skLineSegment(sketch, "E670", {"start": v(1.71, -0.3) * mm, "end": v(1.67, -0.33) * mm});
            skLineSegment(sketch, "E671", {"start": v(1.67, -0.33) * mm, "end": v(1.65, -0.33) * mm});
            skLineSegment(sketch, "E672", {"start": v(1.65, -0.33) * mm, "end": v(1.65, -0.33) * mm});
            skLineSegment(sketch, "E673", {"start": v(2.96, -0.22) * mm, "end": v(2.95, -0.22) * mm});
            skLineSegment(sketch, "E674", {"start": v(2.95, -0.22) * mm, "end": v(2.9, -0.2) * mm});
            skLineSegment(sketch, "E675", {"start": v(2.9, -0.2) * mm, "end": v(2.87, -0.17) * mm});
            skLineSegment(sketch, "E676", {"start": v(2.87, -0.17) * mm, "end": v(2.84, -0.11) * mm});
            skLineSegment(sketch, "E677", {"start": v(2.84, -0.11) * mm, "end": v(2.83, -0.06) * mm});
            skLineSegment(sketch, "E678", {"start": v(2.83, -0.06) * mm, "end": v(2.83, -0.05) * mm});
            skLineSegment(sketch, "E679", {"start": v(2.83, -0.05) * mm, "end": v(2.83, -0.03) * mm});
            skLineSegment(sketch, "E680", {"start": v(2.83, -0.03) * mm, "end": v(2.84, 0.02) * mm});
            skLineSegment(sketch, "E681", {"start": v(2.84, 0.02) * mm, "end": v(2.86, 0.06) * mm});
            skLineSegment(sketch, "E682", {"start": v(2.86, 0.06) * mm, "end": v(2.87, 0.07) * mm});
            skLineSegment(sketch, "E683", {"start": v(2.87, 0.07) * mm, "end": v(2.87, 0.08) * mm});
            skLineSegment(sketch, "E684", {"start": v(2.87, 0.08) * mm, "end": v(2.91, 0.1) * mm});
            skLineSegment(sketch, "E685", {"start": v(2.91, 0.1) * mm, "end": v(2.95, 0.12) * mm});
            skLineSegment(sketch, "E686", {"start": v(2.95, 0.12) * mm, "end": v(2.97, 0.12) * mm});
            skLineSegment(sketch, "E687", {"start": v(2.97, 0.12) * mm, "end": v(2.97, 0.12) * mm});
            skLineSegment(sketch, "E688", {"start": v(2.97, 0.12) * mm, "end": v(2.99, 0.12) * mm});
            skLineSegment(sketch, "E689", {"start": v(2.99, 0.12) * mm, "end": v(3.03, 0.1) * mm});
            skLineSegment(sketch, "E690", {"start": v(3.03, 0.1) * mm, "end": v(3.07, 0.07) * mm});
            skLineSegment(sketch, "E691", {"start": v(3.07, 0.07) * mm, "end": v(3.1, 0.02) * mm});
            skLineSegment(sketch, "E692", {"start": v(3.1, 0.02) * mm, "end": v(3.1, -0.03) * mm});
            skLineSegment(sketch, "E693", {"start": v(3.1, -0.03) * mm, "end": v(3.1, -0.05) * mm});
            skLineSegment(sketch, "E694", {"start": v(3.1, -0.05) * mm, "end": v(3.1, -0.06) * mm});
            skLineSegment(sketch, "E695", {"start": v(3.1, -0.06) * mm, "end": v(3.1, -0.11) * mm});
            skLineSegment(sketch, "E696", {"start": v(3.1, -0.11) * mm, "end": v(3.08, -0.16) * mm});
            skLineSegment(sketch, "E697", {"start": v(3.08, -0.16) * mm, "end": v(3.07, -0.17) * mm});
            skLineSegment(sketch, "E698", {"start": v(3.07, -0.17) * mm, "end": v(3.06, -0.18) * mm});
            skLineSegment(sketch, "E699", {"start": v(3.06, -0.18) * mm, "end": v(3.02, -0.2) * mm});
            skLineSegment(sketch, "E700", {"start": v(3.02, -0.2) * mm, "end": v(2.98, -0.22) * mm});
            skLineSegment(sketch, "E701", {"start": v(2.98, -0.22) * mm, "end": v(2.97, -0.22) * mm});
            skLineSegment(sketch, "E702", {"start": v(2.97, -0.22) * mm, "end": v(2.96, -0.22) * mm});
            skLineSegment(sketch, "E703", {"start": v(3.12, 0.9) * mm, "end": v(3.12, 0.92) * mm});
            skLineSegment(sketch, "E704", {"start": v(3.12, 0.92) * mm, "end": v(3.09, 0.96) * mm});
            skLineSegment(sketch, "E705", {"start": v(3.09, 0.96) * mm, "end": v(3.03, 1) * mm});
            skLineSegment(sketch, "E706", {"start": v(3.03, 1) * mm, "end": v(2.95, 1.02) * mm});
            skLineSegment(sketch, "E707", {"start": v(2.95, 1.02) * mm, "end": v(2.89, 1.04) * mm});
            skLineSegment(sketch, "E708", {"start": v(2.88, 1.04) * mm, "end": v(2.86, 1.03) * mm});
            skLineSegment(sketch, "E709", {"start": v(2.86, 1.03) * mm, "end": v(2.8, 0.99) * mm});
            skLineSegment(sketch, "E710", {"start": v(2.8, 0.99) * mm, "end": v(2.68, 0.93) * mm});
            skLineSegment(sketch, "E711", {"start": v(2.68, 0.93) * mm, "end": v(2.53, 0.87) * mm});
            skLineSegment(sketch, "E712", {"start": v(2.53, 0.87) * mm, "end": v(2.39, 0.84) * mm});
            skLineSegment(sketch, "E713", {"start": v(2.39, 0.84) * mm, "end": v(2.34, 0.83) * mm});
            skLineSegment(sketch, "E714", {"start": v(2.34, 0.83) * mm, "end": v(2.26, 0.82) * mm});
            skLineSegment(sketch, "E715", {"start": v(2.26, 0.82) * mm, "end": v(2.02, 0.8) * mm});
            skLineSegment(sketch, "E716", {"start": v(2.02, 0.8) * mm, "end": v(1.72, 0.79) * mm});
            skLineSegment(sketch, "E717", {"start": v(1.72, 0.79) * mm, "end": v(1.43, 0.8) * mm});
            skLineSegment(sketch, "E718", {"start": v(1.43, 0.8) * mm, "end": v(1.17, 0.83) * mm});
            skLineSegment(sketch, "E719", {"start": v(1.17, 0.83) * mm, "end": v(0.93, 0.88) * mm});
            skLineSegment(sketch, "E720", {"start": v(0.93, 0.88) * mm, "end": v(0.73, 0.94) * mm});
            skLineSegment(sketch, "E721", {"start": v(0.73, 0.94) * mm, "end": v(0.56, 1.01) * mm});
            skLineSegment(sketch, "E722", {"start": v(0.56, 1.01) * mm, "end": v(0.47, 1.07) * mm});
            skLineSegment(sketch, "E723", {"start": v(0.47, 1.07) * mm, "end": v(0.44, 1.1) * mm});
            skLineSegment(sketch, "E724", {"start": v(0.44, 1.1) * mm, "end": v(0.43, 1.1) * mm});
            skLineSegment(sketch, "E725", {"start": v(0.43, 1.1) * mm, "end": v(0.37, 1.09) * mm});
            skLineSegment(sketch, "E726", {"start": v(0.37, 1.09) * mm, "end": v(0.3, 1.07) * mm});
            skLineSegment(sketch, "E727", {"start": v(0.3, 1.07) * mm, "end": v(0.22, 1.03) * mm});
            skLineSegment(sketch, "E728", {"start": v(0.22, 1.03) * mm, "end": v(0.18, 1) * mm});
            skLineSegment(sketch, "E729", {"start": v(0.18, 1) * mm, "end": v(0.18, 0.98) * mm});
            skLineSegment(sketch, "E730", {"start": v(0.18, 0.98) * mm, "end": v(0.17, 0.96) * mm});
            skLineSegment(sketch, "E731", {"start": v(0.17, 0.96) * mm, "end": v(0.18, 0.9) * mm});
            skLineSegment(sketch, "E732", {"start": v(0.18, 0.9) * mm, "end": v(0.23, 0.85) * mm});
            skLineSegment(sketch, "E733", {"start": v(0.23, 0.85) * mm, "end": v(0.25, 0.84) * mm});
            skLineSegment(sketch, "E734", {"start": v(0.25, 0.84) * mm, "end": v(0.27, 0.82) * mm});
            skLineSegment(sketch, "E735", {"start": v(0.27, 0.82) * mm, "end": v(0.33, 0.77) * mm});
            skLineSegment(sketch, "E736", {"start": v(0.33, 0.77) * mm, "end": v(0.44, 0.71) * mm});
            skLineSegment(sketch, "E737", {"start": v(0.44, 0.71) * mm, "end": v(0.58, 0.66) * mm});
            skLineSegment(sketch, "E738", {"start": v(0.58, 0.66) * mm, "end": v(0.75, 0.61) * mm});
            skLineSegment(sketch, "E739", {"start": v(0.75, 0.61) * mm, "end": v(0.95, 0.57) * mm});
            skLineSegment(sketch, "E740", {"start": v(0.95, 0.57) * mm, "end": v(1.2, 0.54) * mm});
            skLineSegment(sketch, "E741", {"start": v(1.2, 0.54) * mm, "end": v(1.5, 0.52) * mm});
            skLineSegment(sketch, "E742", {"start": v(1.5, 0.52) * mm, "end": v(1.75, 0.51) * mm});
            skLineSegment(sketch, "E743", {"start": v(1.75, 0.51) * mm, "end": v(1.84, 0.51) * mm});
            skLineSegment(sketch, "E744", {"start": v(1.84, 0.51) * mm, "end": v(1.84, 0.51) * mm});
            skLineSegment(sketch, "E745", {"start": v(1.84, 0.51) * mm, "end": v(1.87, 0.51) * mm});
            skLineSegment(sketch, "E746", {"start": v(1.87, 0.51) * mm, "end": v(1.98, 0.52) * mm});
            skLineSegment(sketch, "E747", {"start": v(1.98, 0.52) * mm, "end": v(2.14, 0.53) * mm});
            skLineSegment(sketch, "E748", {"start": v(2.14, 0.53) * mm, "end": v(2.3, 0.54) * mm});
            skLineSegment(sketch, "E749", {"start": v(2.3, 0.54) * mm, "end": v(2.48, 0.56) * mm});
            skLineSegment(sketch, "E750", {"start": v(2.48, 0.56) * mm, "end": v(2.65, 0.6) * mm});
            skLineSegment(sketch, "E751", {"start": v(2.65, 0.6) * mm, "end": v(2.81, 0.64) * mm});
            skLineSegment(sketch, "E752", {"start": v(2.81, 0.64) * mm, "end": v(2.95, 0.7) * mm});
            skLineSegment(sketch, "E753", {"start": v(2.95, 0.7) * mm, "end": v(3.04, 0.75) * mm});
            skLineSegment(sketch, "E754", {"start": v(3.04, 0.75) * mm, "end": v(3.06, 0.77) * mm});
            skLineSegment(sketch, "E755", {"start": v(3.06, 0.77) * mm, "end": v(3.07, 0.78) * mm});
            skLineSegment(sketch, "E756", {"start": v(3.07, 0.78) * mm, "end": v(3.12, 0.84) * mm});
            skLineSegment(sketch, "E757", {"start": v(3.12, 0.84) * mm, "end": v(3.12, 0.9) * mm});
            skLineSegment(sketch, "E758", {"start": v(3.12, 0.9) * mm, "end": v(3.12, 0.9) * mm});
            skLineSegment(sketch, "E759", {"start": v(2.33, 2) * mm, "end": v(2.38, 2.01) * mm});
            skLineSegment(sketch, "E760", {"start": v(2.38, 2.01) * mm, "end": v(2.6, 2.05) * mm});
            skLineSegment(sketch, "E761", {"start": v(2.6, 2.05) * mm, "end": v(2.78, 2.1) * mm});
            skLineSegment(sketch, "E762", {"start": v(2.78, 2.1) * mm, "end": v(2.8, 2.1) * mm});
            skLineSegment(sketch, "E763", {"start": v(2.8, 2.1) * mm, "end": v(2.82, 2.1) * mm});
            skLineSegment(sketch, "E764", {"start": v(2.82, 2.1) * mm, "end": v(2.85, 2.12) * mm});
            skLineSegment(sketch, "E765", {"start": v(2.85, 2.12) * mm, "end": v(2.87, 2.15) * mm});
            skLineSegment(sketch, "E766", {"start": v(2.87, 2.15) * mm, "end": v(2.87, 2.15) * mm});
            skLineSegment(sketch, "E767", {"start": v(2.87, 2.15) * mm, "end": v(2.87, 2.16) * mm});
            skLineSegment(sketch, "E768", {"start": v(2.87, 2.16) * mm, "end": v(2.85, 2.18) * mm});
            skLineSegment(sketch, "E769", {"start": v(2.85, 2.18) * mm, "end": v(2.83, 2.2) * mm});
            skLineSegment(sketch, "E770", {"start": v(2.83, 2.2) * mm, "end": v(2.82, 2.2) * mm});
            skLineSegment(sketch, "E771", {"start": v(2.82, 2.2) * mm, "end": v(2.78, 2.23) * mm});
            skLineSegment(sketch, "E772", {"start": v(2.78, 2.23) * mm, "end": v(2.65, 2.3) * mm});
            skLineSegment(sketch, "E773", {"start": v(2.65, 2.3) * mm, "end": v(2.41, 2.38) * mm});
            skLineSegment(sketch, "E774", {"start": v(2.41, 2.38) * mm, "end": v(2.1, 2.45) * mm});
            skLineSegment(sketch, "E775", {"start": v(2.1, 2.45) * mm, "end": v(1.8, 2.48) * mm});
            skLineSegment(sketch, "E776", {"start": v(1.8, 2.48) * mm, "end": v(1.7, 2.49) * mm});
            skLineSegment(sketch, "E777", {"start": v(1.7, 2.49) * mm, "end": v(1.68, 2.49) * mm});
            skLineSegment(sketch, "E778", {"start": v(1.68, 2.49) * mm, "end": v(1.57, 2.5) * mm});
            skLineSegment(sketch, "E779", {"start": v(1.57, 2.5) * mm, "end": v(1.25, 2.47) * mm});
            skLineSegment(sketch, "E780", {"start": v(1.25, 2.47) * mm, "end": v(0.94, 2.42) * mm});
            skLineSegment(sketch, "E781", {"start": v(0.94, 2.42) * mm, "end": v(0.72, 2.35) * mm});
            skLineSegment(sketch, "E782", {"start": v(0.72, 2.35) * mm, "end": v(0.61, 2.3) * mm});
            skLineSegment(sketch, "E783", {"start": v(0.61, 2.3) * mm, "end": v(0.58, 2.28) * mm});
            skLineSegment(sketch, "E784", {"start": v(0.58, 2.28) * mm, "end": v(0.57, 2.28) * mm});
            skLineSegment(sketch, "E785", {"start": v(0.57, 2.28) * mm, "end": v(0.55, 2.25) * mm});
            skLineSegment(sketch, "E786", {"start": v(0.55, 2.25) * mm, "end": v(0.54, 2.24) * mm});
            skLineSegment(sketch, "E787", {"start": v(0.54, 2.24) * mm, "end": v(0.54, 2.23) * mm});
            skLineSegment(sketch, "E788", {"start": v(0.54, 2.23) * mm, "end": v(0.54, 2.22) * mm});
            skLineSegment(sketch, "E789", {"start": v(0.54, 2.22) * mm, "end": v(0.55, 2.2) * mm});
            skLineSegment(sketch, "E790", {"start": v(0.55, 2.2) * mm, "end": v(0.58, 2.18) * mm});
            skLineSegment(sketch, "E791", {"start": v(0.58, 2.18) * mm, "end": v(0.59, 2.18) * mm});
            skLineSegment(sketch, "E792", {"start": v(0.59, 2.18) * mm, "end": v(0.66, 2.14) * mm});
            skLineSegment(sketch, "E793", {"start": v(0.66, 2.14) * mm, "end": v(0.9, 2.07) * mm});
            skLineSegment(sketch, "E794", {"start": v(0.9, 2.07) * mm, "end": v(1.3, 2) * mm});
            skLineSegment(sketch, "E795", {"start": v(1.3, 2) * mm, "end": v(1.79, 1.98) * mm});
            skLineSegment(sketch, "E796", {"start": v(1.79, 1.98) * mm, "end": v(2.2, 2) * mm});
            skLineSegment(sketch, "E797", {"start": v(2.2, 2) * mm, "end": v(2.33, 2) * mm});
            skLineSegment(sketch, "E798", {"start": v(1.82, 1.84) * mm, "end": v(1.7, 1.84) * mm});
            skLineSegment(sketch, "E799", {"start": v(1.7, 1.84) * mm, "end": v(1.35, 1.87) * mm});
            skLineSegment(sketch, "E800", {"start": v(1.35, 1.87) * mm, "end": v(1, 1.92) * mm});
            skLineSegment(sketch, "E801", {"start": v(1, 1.92) * mm, "end": v(0.73, 2) * mm});
            skLineSegment(sketch, "E802", {"start": v(0.73, 2) * mm, "end": v(0.57, 2.05) * mm});
            skLineSegment(sketch, "E803", {"start": v(0.57, 2.05) * mm, "end": v(0.52, 2.07) * mm});
            skLineSegment(sketch, "E804", {"start": v(0.52, 2.07) * mm, "end": v(0.5, 1.21) * mm});
            skLineSegment(sketch, "E805", {"start": v(0.5, 1.21) * mm, "end": v(0.51, 1.2) * mm});
            skLineSegment(sketch, "E806", {"start": v(0.51, 1.2) * mm, "end": v(0.57, 1.16) * mm});
            skLineSegment(sketch, "E807", {"start": v(0.57, 1.16) * mm, "end": v(0.69, 1.1) * mm});
            skLineSegment(sketch, "E808", {"start": v(0.69, 1.1) * mm, "end": v(0.84, 1.05) * mm});
            skLineSegment(sketch, "E809", {"start": v(0.84, 1.05) * mm, "end": v(1.03, 1) * mm});
            skLineSegment(sketch, "E810", {"start": v(1.03, 1) * mm, "end": v(1.27, 0.96) * mm});
            skLineSegment(sketch, "E811", {"start": v(1.27, 0.96) * mm, "end": v(1.54, 0.94) * mm});
            skLineSegment(sketch, "E812", {"start": v(1.54, 0.94) * mm, "end": v(1.85, 0.94) * mm});
            skLineSegment(sketch, "E813", {"start": v(1.85, 0.94) * mm, "end": v(2.12, 0.95) * mm});
            skLineSegment(sketch, "E814", {"start": v(2.12, 0.95) * mm, "end": v(2.21, 0.96) * mm});
            skLineSegment(sketch, "E815", {"start": v(2.21, 0.96) * mm, "end": v(2.27, 0.97) * mm});
            skLineSegment(sketch, "E816", {"start": v(2.27, 0.97) * mm, "end": v(2.43, 1) * mm});
            skLineSegment(sketch, "E817", {"start": v(2.43, 1) * mm, "end": v(2.62, 1.05) * mm});
            skLineSegment(sketch, "E818", {"start": v(2.62, 1.05) * mm, "end": v(2.75, 1.1) * mm});
            skLineSegment(sketch, "E819", {"start": v(2.75, 1.1) * mm, "end": v(2.83, 1.15) * mm});
            skLineSegment(sketch, "E820", {"start": v(2.83, 1.15) * mm, "end": v(2.85, 1.17) * mm});
            skLineSegment(sketch, "E821", {"start": v(2.85, 1.17) * mm, "end": v(2.88, 1.99) * mm});
            skLineSegment(sketch, "E822", {"start": v(2.88, 1.99) * mm, "end": v(2.82, 1.96) * mm});
            skLineSegment(sketch, "E823", {"start": v(2.82, 1.96) * mm, "end": v(2.63, 1.91) * mm});
            skLineSegment(sketch, "E824", {"start": v(2.63, 1.91) * mm, "end": v(2.34, 1.87) * mm});
            skLineSegment(sketch, "E825", {"start": v(2.34, 1.87) * mm, "end": v(2.06, 1.85) * mm});
            skLineSegment(sketch, "E826", {"start": v(2.06, 1.85) * mm, "end": v(1.88, 1.84) * mm});
            skLineSegment(sketch, "E827", {"start": v(1.88, 1.84) * mm, "end": v(1.82, 1.84) * mm});
            skCircle(sketch, "E828", {"center": v(0, 0) * mm, "radius": 5 * mm});
            skLineSegment(sketch, "E829", {"start": v(2.92, -0.96) * mm, "end": v(2.95, -0.95) * mm});
            skLineSegment(sketch, "E830", {"start": v(1.84, -1.1) * mm, "end": v(1.78, -1.03) * mm});
            skLineSegment(sketch, "E831", {"start": v(2.88, 1.04) * mm, "end": v(2.89, 1.04) * mm});
            skSolve(sketch);
        }
        {
            var Q0;
            Q0=makeQuery(id+"F0.imprint","IMPRINT",FACE,{"disambiguationData":[TD([[makeQuery(id+"F0.imprint","IMPRINT",EDGE,{"derivedFrom":sQuery(id+"F0.wireOp",EDGE,"E0")}),1.0]])]});
            extrude(context, id + "F1", {"entities" : qUnion([Q0]), "depth" : 4 * mm});
        }
        {
            var Q0;
            Q0=makeQuery(id+"F0.imprint","IMPRINT",FACE,{"disambiguationData":[TD([[makeQuery(id+"F0.imprint","IMPRINT",EDGE,{"derivedFrom":sQuery(id+"F0.wireOp",EDGE,"E419")}),-1.0]])]});
            extrude(context, id + "F2", {"entities" : qUnion([Q0]), "operationType" : NewBodyOperationType.ADD, "depth" : 5 * mm});
        }
        {
            var Q0;
            Q0=makeQuery(id+"F0.imprint","IMPRINT",FACE,{"disambiguationData":[TD([[makeQuery(id+"F0.imprint","IMPRINT",EDGE,{"derivedFrom":sQuery(id+"F0.wireOp",EDGE,"E798")}),1.0]])]});
            var Q1;
            Q1=makeQuery(id+"F0.imprint","IMPRINT",FACE,{"disambiguationData":[TD([[makeQuery(id+"F0.imprint","IMPRINT",EDGE,{"derivedFrom":sQuery(id+"F0.wireOp",EDGE,"E703")}),1.0]])]});
            var Q2;
            Q2=makeQuery(id+"F0.imprint","IMPRINT",FACE,{"disambiguationData":[TD([[makeQuery(id+"F0.imprint","IMPRINT",EDGE,{"derivedFrom":sQuery(id+"F0.wireOp",EDGE,"E759")}),1.0]])]});
            extrude(context, id + "F3", {"entities" : qUnion([Q0, Q1, Q2]), "operationType" : NewBodyOperationType.ADD, "depth" : 5 * mm});
        }
        {
            var Q0;
            Q0=makeQuery(id+"F0.imprint","IMPRINT",FACE,{"disambiguationData":[TD([[makeQuery(id+"F0.imprint","IMPRINT",EDGE,{"derivedFrom":sQuery(id+"F0.wireOp",EDGE,"E0")}),-1.0]])]});
            extrude(context, id + "F4", {"entities" : qUnion([Q0]), "operationType" : NewBodyOperationType.ADD, "depth" : 3.5 * mm});
        }
        {
            var Q0;
            Q0=makeQuery(id+"F0.imprint","IMPRINT",FACE,{"disambiguationData":[TD([[makeQuery(id+"F0.imprint","IMPRINT",EDGE,{"derivedFrom":sQuery(id+"F0.wireOp",EDGE,"E644")}),-1.0]])]});
            var Q1;
            Q1=makeQuery(id+"F0.imprint","IMPRINT",FACE,{"disambiguationData":[TD([[makeQuery(id+"F0.imprint","IMPRINT",EDGE,{"derivedFrom":sQuery(id+"F0.wireOp",EDGE,"E673")}),-1.0]])]});
            extrude(context, id + "F5", {"entities" : qUnion([Q0, Q1]), "operationType" : NewBodyOperationType.ADD, "depth" : 3 * mm});
        }
        {
            var Q0;
            Q0=makeQuery(id+"F0.imprint","IMPRINT",FACE,{"disambiguationData":[TD([[makeQuery(id+"F0.imprint","IMPRINT",EDGE,{"derivedFrom":sQuery(id+"F0.wireOp",EDGE,"E532")}),1.0]])]});
            extrude(context, id + "F6", {"entities" : qUnion([Q0]), "operationType" : NewBodyOperationType.ADD, "depth" : 3.5 * mm});
        }
    });
